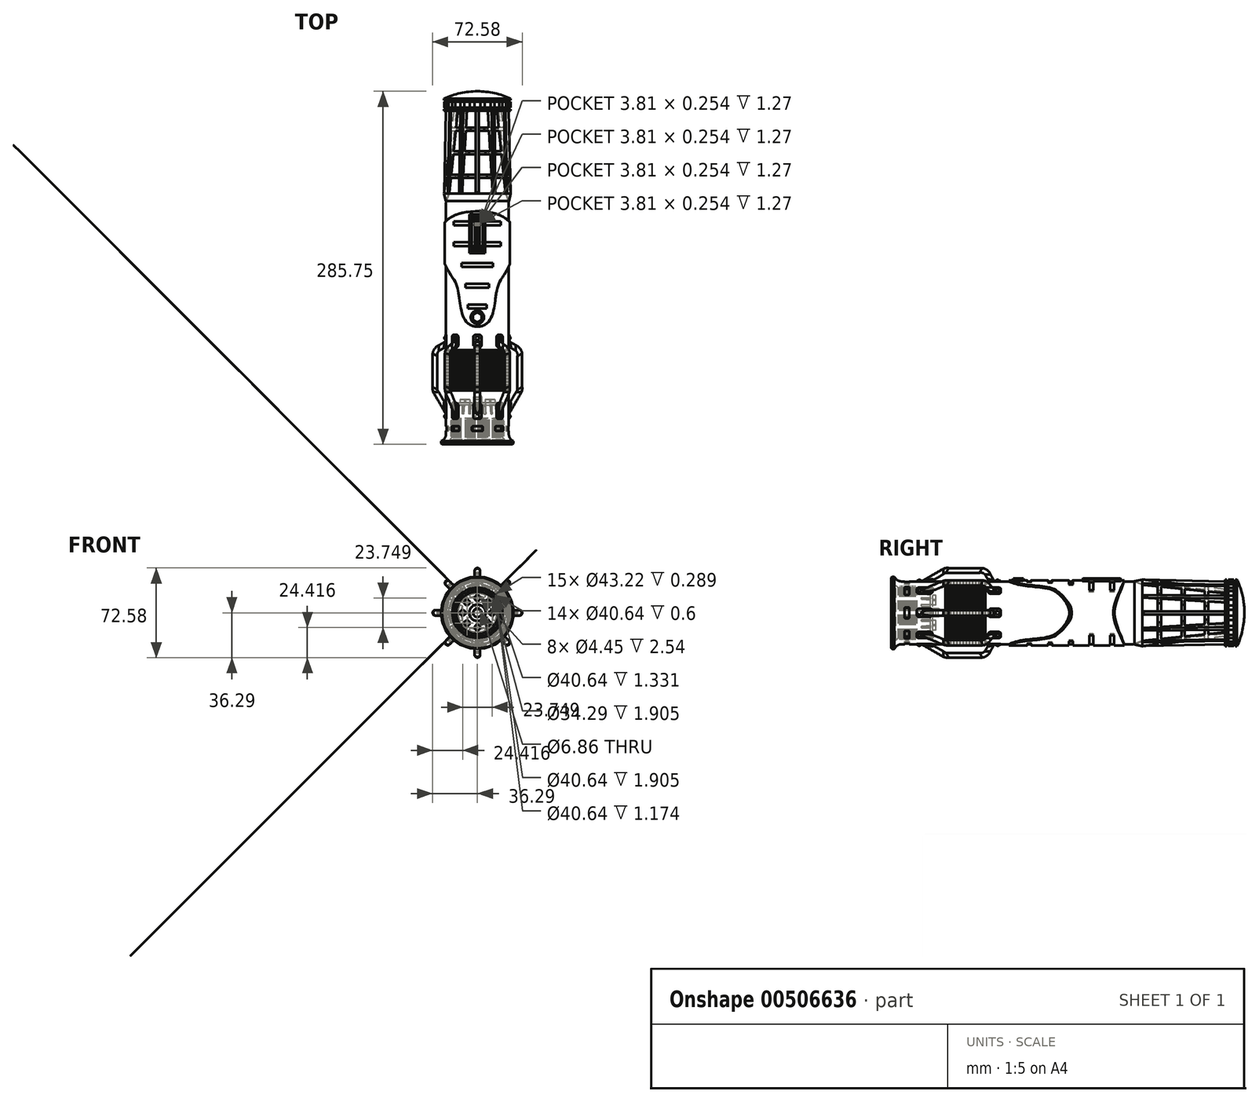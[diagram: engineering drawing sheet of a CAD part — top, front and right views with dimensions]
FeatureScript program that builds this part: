
annotation { "Feature Type Name" : "Feature", "Feature Type Description" : "" }
export const myFeature = defineFeature(function(context is Context, id is Id, definition is map)
    precondition{}
    {
        {
            var Q0;
            Q0=qCreatedBy(makeId("Right.planeOp"),FACE);
            var sketch = newSketch(context, id + "F0", { "sketchPlane" : qUnion([Q0])});
            skLineSegment(sketch, "E0", {"start": v(44.04, 0) * mm, "end": v(254, 0) * mm});
            skLineSegment(sketch, "E1", {"start": v(270.13, 19.05) * mm, "end": v(256.42, 20.68) * mm});
            skLineSegment(sketch, "E2", {"start": v(203, 27.02) * mm, "end": v(196.97, 25.65) * mm});
            skLineSegment(sketch, "E3", {"start": v(195.42, 25.4) * mm, "end": v(76.16, 25.4) * mm});
            skLineSegment(sketch, "E4", {"start": v(0, 25.4) * mm, "end": v(0, 20.32) * mm});
            skLineSegment(sketch, "E5", {"start": v(254, 0) * mm, "end": v(285.75, 0) * mm});
            skPoint(sketch, "E6.visualSharp", {"position": v(270.13, 19.05) * mm});
            skLineSegment(sketch, "E7", {"start": v(0, 25.4) * mm, "end": v(0, 29.21) * mm});
            skLineSegment(sketch, "E8", {"start": v(0, 29.21) * mm, "end": v(2.54, 29.21) * mm});
            skLineSegment(sketch, "E9", {"start": v(2.54, 29.21) * mm, "end": v(4.74, 25.4) * mm});
            skLineSegment(sketch, "E10", {"start": v(31.75, 3.43) * mm, "end": v(31.75, 6.6) * mm});
            skLineSegment(sketch, "E11", {"start": v(20.95, 20.32) * mm, "end": v(19.62, 20.32) * mm});
            skLineSegment(sketch, "E12", {"start": v(1.9, 20.32) * mm, "end": v(3.8, 22.23) * mm});
            skLineSegment(sketch, "E13", {"start": v(3.81, 22.23) * mm, "end": v(5.72, 20.32) * mm});
            skLineSegment(sketch, "E14", {"start": v(6.89, 20.32) * mm, "end": v(6.89, 21.61) * mm});
            skLineSegment(sketch, "E15", {"start": v(6.89, 21.61) * mm, "end": v(7.18, 21.61) * mm});
            skLineSegment(sketch, "E16", {"start": v(7.18, 21.61) * mm, "end": v(7.18, 20.32) * mm});
            skLineSegment(sketch, "E17.1.0.0", {"start": v(7.78, 20.32) * mm, "end": v(7.78, 21.61) * mm});
            skLineSegment(sketch, "E17.1.0.1", {"start": v(7.78, 21.61) * mm, "end": v(8.07, 21.61) * mm});
            skLineSegment(sketch, "E17.1.0.2", {"start": v(8.07, 21.61) * mm, "end": v(8.07, 20.32) * mm});
            skLineSegment(sketch, "E17.2.0.0", {"start": v(8.67, 20.32) * mm, "end": v(8.67, 21.61) * mm});
            skLineSegment(sketch, "E17.2.0.1", {"start": v(8.67, 21.61) * mm, "end": v(8.96, 21.61) * mm});
            skLineSegment(sketch, "E17.2.0.2", {"start": v(8.96, 21.61) * mm, "end": v(8.96, 20.32) * mm});
            skLineSegment(sketch, "E17.3.0.0", {"start": v(9.56, 20.32) * mm, "end": v(9.56, 21.61) * mm});
            skLineSegment(sketch, "E17.3.0.1", {"start": v(9.56, 21.61) * mm, "end": v(9.85, 21.61) * mm});
            skLineSegment(sketch, "E17.3.0.2", {"start": v(9.85, 21.61) * mm, "end": v(9.85, 20.32) * mm});
            skLineSegment(sketch, "E17.4.0.0", {"start": v(10.45, 20.32) * mm, "end": v(10.45, 21.61) * mm});
            skLineSegment(sketch, "E17.4.0.1", {"start": v(10.45, 21.61) * mm, "end": v(10.73, 21.61) * mm});
            skLineSegment(sketch, "E17.4.0.2", {"start": v(10.73, 21.61) * mm, "end": v(10.73, 20.32) * mm});
            skLineSegment(sketch, "E17.5.0.0", {"start": v(11.33, 20.32) * mm, "end": v(11.33, 21.61) * mm});
            skLineSegment(sketch, "E17.5.0.1", {"start": v(11.33, 21.61) * mm, "end": v(11.62, 21.61) * mm});
            skLineSegment(sketch, "E17.5.0.2", {"start": v(11.62, 21.61) * mm, "end": v(11.62, 20.32) * mm});
            skLineSegment(sketch, "E17.6.0.0", {"start": v(12.22, 20.32) * mm, "end": v(12.22, 21.61) * mm});
            skLineSegment(sketch, "E17.6.0.1", {"start": v(12.22, 21.61) * mm, "end": v(12.51, 21.61) * mm});
            skLineSegment(sketch, "E17.6.0.2", {"start": v(12.51, 21.61) * mm, "end": v(12.51, 20.32) * mm});
            skLineSegment(sketch, "E17.7.0.0", {"start": v(13.11, 20.32) * mm, "end": v(13.11, 21.61) * mm});
            skLineSegment(sketch, "E17.7.0.1", {"start": v(13.11, 21.61) * mm, "end": v(13.4, 21.61) * mm});
            skLineSegment(sketch, "E17.7.0.2", {"start": v(13.4, 21.61) * mm, "end": v(13.4, 20.32) * mm});
            skLineSegment(sketch, "E17.8.0.0", {"start": v(14, 20.32) * mm, "end": v(14, 21.61) * mm});
            skLineSegment(sketch, "E17.8.0.1", {"start": v(14, 21.61) * mm, "end": v(14.3, 21.61) * mm});
            skLineSegment(sketch, "E17.8.0.2", {"start": v(14.3, 21.61) * mm, "end": v(14.3, 20.32) * mm});
            skLineSegment(sketch, "E17.9.0.0", {"start": v(14.9, 20.32) * mm, "end": v(14.9, 21.61) * mm});
            skLineSegment(sketch, "E17.9.0.1", {"start": v(14.9, 21.61) * mm, "end": v(15.18, 21.61) * mm});
            skLineSegment(sketch, "E17.9.0.2", {"start": v(15.18, 21.61) * mm, "end": v(15.18, 20.32) * mm});
            skLineSegment(sketch, "E17.10.0.0", {"start": v(15.78, 20.32) * mm, "end": v(15.78, 21.61) * mm});
            skLineSegment(sketch, "E17.10.0.1", {"start": v(15.78, 21.61) * mm, "end": v(16.07, 21.61) * mm});
            skLineSegment(sketch, "E17.10.0.2", {"start": v(16.07, 21.61) * mm, "end": v(16.07, 20.32) * mm});
            skLineSegment(sketch, "E17.11.0.0", {"start": v(16.67, 20.32) * mm, "end": v(16.67, 21.61) * mm});
            skLineSegment(sketch, "E17.11.0.1", {"start": v(16.67, 21.61) * mm, "end": v(16.96, 21.61) * mm});
            skLineSegment(sketch, "E17.11.0.2", {"start": v(16.96, 21.61) * mm, "end": v(16.96, 20.32) * mm});
            skLineSegment(sketch, "E17.12.0.0", {"start": v(17.56, 20.32) * mm, "end": v(17.56, 21.61) * mm});
            skLineSegment(sketch, "E17.12.0.1", {"start": v(17.56, 21.61) * mm, "end": v(17.85, 21.61) * mm});
            skLineSegment(sketch, "E17.12.0.2", {"start": v(17.85, 21.61) * mm, "end": v(17.85, 20.32) * mm});
            skLineSegment(sketch, "E17.13.0.0", {"start": v(18.45, 20.32) * mm, "end": v(18.45, 21.61) * mm});
            skLineSegment(sketch, "E17.13.0.1", {"start": v(18.45, 21.61) * mm, "end": v(18.74, 21.61) * mm});
            skLineSegment(sketch, "E17.13.0.2", {"start": v(18.74, 21.61) * mm, "end": v(18.74, 20.32) * mm});
            skLineSegment(sketch, "E17.14.0.0", {"start": v(19.34, 20.32) * mm, "end": v(19.34, 21.61) * mm});
            skLineSegment(sketch, "E17.14.0.1", {"start": v(19.34, 21.61) * mm, "end": v(19.62, 21.61) * mm});
            skLineSegment(sketch, "E17.14.0.2", {"start": v(19.62, 21.61) * mm, "end": v(19.62, 20.32) * mm});
            skLineSegment(sketch, "E17.direction1", {"start": v(7.18, 20.32) * mm, "end": v(7.78, 20.32) * mm, "construction": true});
            skLineSegment(sketch, "E18", {"start": v(31.75, 3.43) * mm, "end": v(38.1, 3.43) * mm});
            skLineSegment(sketch, "E19", {"start": v(38.1, 3.43) * mm, "end": v(44.04, 0) * mm});
            skLineSegment(sketch, "E20.bottom", {"start": v(31.75, 17.15) * mm, "end": v(33.65, 17.15) * mm});
            skLineSegment(sketch, "E20.top", {"start": v(31.75, 6.6) * mm, "end": v(33.65, 6.6) * mm});
            skLineSegment(sketch, "E20.right", {"start": v(33.65, 17.15) * mm, "end": v(33.65, 6.6) * mm});
            skLineSegment(sketch, "E21", {"start": v(31.75, 18.42) * mm, "end": v(20.95, 20.32) * mm});
            skPoint(sketch, "E22.orphan", {"position": v(31.75, 20.32) * mm});
            skLineSegment(sketch, "E23.trimOffspring", {"start": v(31.75, 17.15) * mm, "end": v(31.75, 18.42) * mm});
            skLineSegment(sketch, "E24.trimOffspring", {"start": v(6.89, 20.32) * mm, "end": v(5.71, 20.32) * mm});
            skLineSegment(sketch, "E25.trimOffspring", {"start": v(7.78, 20.32) * mm, "end": v(7.18, 20.32) * mm});
            skLineSegment(sketch, "E26.trimOffspring", {"start": v(8.67, 20.32) * mm, "end": v(8.07, 20.32) * mm});
            skLineSegment(sketch, "E27.trimOffspring", {"start": v(9.56, 20.32) * mm, "end": v(8.96, 20.32) * mm});
            skLineSegment(sketch, "E28.trimOffspring", {"start": v(10.45, 20.32) * mm, "end": v(9.85, 20.32) * mm});
            skLineSegment(sketch, "E29.trimOffspring", {"start": v(11.33, 20.32) * mm, "end": v(10.73, 20.32) * mm});
            skLineSegment(sketch, "E30.trimOffspring", {"start": v(12.22, 20.32) * mm, "end": v(11.62, 20.32) * mm});
            skLineSegment(sketch, "E31.trimOffspring", {"start": v(13.11, 20.32) * mm, "end": v(12.51, 20.32) * mm});
            skLineSegment(sketch, "E32.trimOffspring", {"start": v(14, 20.32) * mm, "end": v(13.4, 20.32) * mm});
            skLineSegment(sketch, "E33.trimOffspring", {"start": v(14.9, 20.32) * mm, "end": v(14.3, 20.32) * mm});
            skLineSegment(sketch, "E34.trimOffspring", {"start": v(15.78, 20.32) * mm, "end": v(15.18, 20.32) * mm});
            skLineSegment(sketch, "E35.trimOffspring", {"start": v(16.67, 20.32) * mm, "end": v(16.07, 20.32) * mm});
            skLineSegment(sketch, "E36.trimOffspring", {"start": v(17.56, 20.32) * mm, "end": v(16.96, 20.32) * mm});
            skLineSegment(sketch, "E37.trimOffspring", {"start": v(18.45, 20.32) * mm, "end": v(17.85, 20.32) * mm});
            skLineSegment(sketch, "E38.trimOffspring", {"start": v(19.34, 20.32) * mm, "end": v(18.74, 20.32) * mm});
            skLineSegment(sketch, "E39.trimOffspring", {"start": v(1.9, 20.32) * mm, "end": v(0, 20.32) * mm});
            skPoint(sketch, "E40.orphan", {"position": v(0, 0) * mm});
            skLineSegment(sketch, "E41.top", {"start": v(44.04, 26.04) * mm, "end": v(45.3, 26.04) * mm});
            skLineSegment(sketch, "E42", {"start": v(44.04, 26.04) * mm, "end": v(43.67, 25.4) * mm});
            skLineSegment(sketch, "E43", {"start": v(75.79, 26.04) * mm, "end": v(76.16, 25.4) * mm});
            skLineSegment(sketch, "E44", {"start": v(45.3, 26.03) * mm, "end": v(45.3, 26.1) * mm});
            skLineSegment(sketch, "E45", {"start": v(45.82, 26.1) * mm, "end": v(45.82, 26.03) * mm});
            skArc(sketch, "E46", {"start": v(45.82, 26.1) * mm, "mid": v(45.56, 26.35) * mm, "end": v(45.3, 26.1) * mm});
            skLineSegment(sketch, "E47.1.0.0", {"start": v(47.85, 26.04) * mm, "end": v(47.85, 26.1) * mm});
            skArc(sketch, "E47.1.0.1", {"start": v(48.36, 26.1) * mm, "mid": v(48.1, 26.35) * mm, "end": v(47.85, 26.1) * mm});
            skLineSegment(sketch, "E47.1.0.2", {"start": v(48.36, 26.1) * mm, "end": v(48.36, 26.04) * mm});
            skLineSegment(sketch, "E47.2.0.0", {"start": v(50.39, 26.04) * mm, "end": v(50.39, 26.1) * mm});
            skArc(sketch, "E47.2.0.1", {"start": v(50.9, 26.1) * mm, "mid": v(50.64, 26.35) * mm, "end": v(50.39, 26.1) * mm});
            skLineSegment(sketch, "E47.2.0.2", {"start": v(50.9, 26.1) * mm, "end": v(50.9, 26.04) * mm});
            skLineSegment(sketch, "E47.3.0.0", {"start": v(52.93, 26.04) * mm, "end": v(52.93, 26.1) * mm});
            skArc(sketch, "E47.3.0.1", {"start": v(53.44, 26.1) * mm, "mid": v(53.18, 26.35) * mm, "end": v(52.93, 26.1) * mm});
            skLineSegment(sketch, "E47.3.0.2", {"start": v(53.44, 26.1) * mm, "end": v(53.44, 26.04) * mm});
            skLineSegment(sketch, "E47.4.0.0", {"start": v(55.47, 26.04) * mm, "end": v(55.47, 26.1) * mm});
            skArc(sketch, "E47.4.0.1", {"start": v(55.98, 26.1) * mm, "mid": v(55.72, 26.35) * mm, "end": v(55.47, 26.1) * mm});
            skLineSegment(sketch, "E47.4.0.2", {"start": v(55.98, 26.1) * mm, "end": v(55.98, 26.04) * mm});
            skLineSegment(sketch, "E47.5.0.0", {"start": v(58, 26.04) * mm, "end": v(58, 26.1) * mm});
            skArc(sketch, "E47.5.0.1", {"start": v(58.52, 26.1) * mm, "mid": v(58.26, 26.35) * mm, "end": v(58, 26.1) * mm});
            skLineSegment(sketch, "E47.5.0.2", {"start": v(58.52, 26.1) * mm, "end": v(58.52, 26.04) * mm});
            skLineSegment(sketch, "E47.6.0.0", {"start": v(60.55, 26.04) * mm, "end": v(60.55, 26.1) * mm});
            skArc(sketch, "E47.6.0.1", {"start": v(61.06, 26.1) * mm, "mid": v(60.8, 26.35) * mm, "end": v(60.55, 26.1) * mm});
            skLineSegment(sketch, "E47.6.0.2", {"start": v(61.06, 26.1) * mm, "end": v(61.06, 26.04) * mm});
            skLineSegment(sketch, "E47.7.0.0", {"start": v(63.09, 26.04) * mm, "end": v(63.09, 26.1) * mm});
            skArc(sketch, "E47.7.0.1", {"start": v(63.6, 26.1) * mm, "mid": v(63.34, 26.35) * mm, "end": v(63.09, 26.1) * mm});
            skLineSegment(sketch, "E47.7.0.2", {"start": v(63.6, 26.1) * mm, "end": v(63.6, 26.04) * mm});
            skLineSegment(sketch, "E47.8.0.0", {"start": v(65.63, 26.04) * mm, "end": v(65.63, 26.1) * mm});
            skArc(sketch, "E47.8.0.1", {"start": v(66.14, 26.1) * mm, "mid": v(65.88, 26.35) * mm, "end": v(65.63, 26.1) * mm});
            skLineSegment(sketch, "E47.8.0.2", {"start": v(66.14, 26.1) * mm, "end": v(66.14, 26.04) * mm});
            skLineSegment(sketch, "E47.9.0.0", {"start": v(68.17, 26.04) * mm, "end": v(68.17, 26.1) * mm});
            skArc(sketch, "E47.9.0.1", {"start": v(68.68, 26.1) * mm, "mid": v(68.42, 26.35) * mm, "end": v(68.17, 26.1) * mm});
            skLineSegment(sketch, "E47.9.0.2", {"start": v(68.68, 26.1) * mm, "end": v(68.68, 26.04) * mm});
            skLineSegment(sketch, "E47.10.0.0", {"start": v(70.7, 26.04) * mm, "end": v(70.7, 26.1) * mm});
            skArc(sketch, "E47.10.0.1", {"start": v(71.22, 26.1) * mm, "mid": v(70.96, 26.35) * mm, "end": v(70.7, 26.1) * mm});
            skLineSegment(sketch, "E47.10.0.2", {"start": v(71.22, 26.1) * mm, "end": v(71.22, 26.04) * mm});
            skLineSegment(sketch, "E47.11.0.0", {"start": v(73.25, 26.04) * mm, "end": v(73.25, 26.1) * mm});
            skArc(sketch, "E47.11.0.1", {"start": v(73.76, 26.1) * mm, "mid": v(73.5, 26.35) * mm, "end": v(73.25, 26.1) * mm});
            skLineSegment(sketch, "E47.11.0.2", {"start": v(73.76, 26.1) * mm, "end": v(73.76, 26.03) * mm});
            skLineSegment(sketch, "E47.direction1", {"start": v(45.3, 26.04) * mm, "end": v(47.85, 26.04) * mm, "construction": true});
            skLineSegment(sketch, "E48.trimOffspring", {"start": v(45.82, 26.04) * mm, "end": v(47.85, 26.04) * mm});
            skLineSegment(sketch, "E49.trimOffspring", {"start": v(48.36, 26.04) * mm, "end": v(50.39, 26.04) * mm});
            skLineSegment(sketch, "E50.trimOffspring", {"start": v(50.9, 26.04) * mm, "end": v(52.93, 26.04) * mm});
            skLineSegment(sketch, "E51.trimOffspring", {"start": v(53.44, 26.04) * mm, "end": v(55.47, 26.04) * mm});
            skLineSegment(sketch, "E52.trimOffspring", {"start": v(55.98, 26.04) * mm, "end": v(58, 26.04) * mm});
            skLineSegment(sketch, "E53.trimOffspring", {"start": v(58.52, 26.04) * mm, "end": v(60.55, 26.04) * mm});
            skLineSegment(sketch, "E54.trimOffspring", {"start": v(61.06, 26.04) * mm, "end": v(63.09, 26.04) * mm});
            skLineSegment(sketch, "E55.trimOffspring", {"start": v(63.6, 26.04) * mm, "end": v(65.63, 26.04) * mm});
            skLineSegment(sketch, "E56.trimOffspring", {"start": v(66.14, 26.04) * mm, "end": v(68.17, 26.04) * mm});
            skLineSegment(sketch, "E57.trimOffspring", {"start": v(68.68, 26.04) * mm, "end": v(70.7, 26.04) * mm});
            skLineSegment(sketch, "E58.trimOffspring", {"start": v(71.22, 26.04) * mm, "end": v(73.25, 26.04) * mm});
            skLineSegment(sketch, "E59.trimOffspring", {"start": v(73.76, 26.04) * mm, "end": v(75.79, 26.04) * mm});
            skLineSegment(sketch, "E60.trimOffspring", {"start": v(43.67, 25.4) * mm, "end": v(4.74, 25.4) * mm});
            skPoint(sketch, "E41.left.start.orphan", {"position": v(44.04, 25.4) * mm});
            skLineSegment(sketch, "E61", {"start": v(196.3, 25.25) * mm, "end": v(203.03, 22.8) * mm});
            skLineSegment(sketch, "E62", {"start": v(203.03, 22.8) * mm, "end": v(203.03, 23.2) * mm});
            skLineSegment(sketch, "E63", {"start": v(203.03, 23.2) * mm, "end": v(196.96, 25.4) * mm});
            skPoint(sketch, "E64.visualSharp", {"position": v(195.87, 25.4) * mm});
            skArc(sketch, "E64.filletArc", {"start": v(196.3, 25.25) * mm, "mid": v(195.86, 25.36) * mm, "end": v(195.42, 25.4) * mm});
            skPoint(sketch, "E65.visualSharp", {"position": v(196.55, 25.56) * mm});
            skArc(sketch, "E65.filletArc", {"start": v(196.97, 25.65) * mm, "mid": v(196.88, 25.54) * mm, "end": v(196.96, 25.4) * mm});
            skArc(sketch, "E66", {"start": v(285.75, 0) * mm, "mid": v(284.22, 13.84) * mm, "end": v(279.71, 27.02) * mm});
            skLineSegment(sketch, "E67", {"start": v(270.13, 19.05) * mm, "end": v(270.13, 27.02) * mm});
            skLineSegment(sketch, "E68", {"start": v(270.13, 27.02) * mm, "end": v(271.4, 27.02) * mm});
            skLineSegment(sketch, "E69", {"start": v(271.4, 27.02) * mm, "end": v(271.4, 24.86) * mm});
            skLineSegment(sketch, "E70", {"start": v(271.4, 24.86) * mm, "end": v(272.67, 24.86) * mm});
            skLineSegment(sketch, "E71", {"start": v(272.67, 24.86) * mm, "end": v(272.67, 27.02) * mm});
            skLineSegment(sketch, "E72", {"start": v(272.67, 27.02) * mm, "end": v(277.17, 27.02) * mm});
            skLineSegment(sketch, "E73", {"start": v(277.17, 27.02) * mm, "end": v(277.17, 24.86) * mm});
            skLineSegment(sketch, "E74", {"start": v(277.17, 24.86) * mm, "end": v(278.44, 24.86) * mm});
            skLineSegment(sketch, "E75", {"start": v(278.44, 24.86) * mm, "end": v(278.44, 27.02) * mm});
            skLineSegment(sketch, "E76.trimOffspring", {"start": v(278.44, 27.02) * mm, "end": v(279.71, 27.02) * mm});
            skLineSegment(sketch, "E77.top", {"start": v(215.7, 17.9) * mm, "end": v(218.32, 17.9) * mm});
            skLineSegment(sketch, "E77.left", {"start": v(215.7, 25.51) * mm, "end": v(215.7, 17.9) * mm});
            skLineSegment(sketch, "E77.right", {"start": v(218.32, 25.2) * mm, "end": v(218.32, 17.9) * mm});
            skLineSegment(sketch, "E78.1.0.0", {"start": v(234.75, 23.25) * mm, "end": v(234.75, 15.63) * mm});
            skLineSegment(sketch, "E78.1.0.1", {"start": v(237.37, 22.94) * mm, "end": v(237.37, 15.63) * mm});
            skLineSegment(sketch, "E78.1.0.2", {"start": v(234.75, 15.63) * mm, "end": v(237.37, 15.63) * mm});
            skLineSegment(sketch, "E78.2.0.0", {"start": v(253.8, 20.99) * mm, "end": v(253.8, 13.37) * mm});
            skLineSegment(sketch, "E78.2.0.1", {"start": v(256.42, 20.68) * mm, "end": v(256.42, 13.37) * mm});
            skLineSegment(sketch, "E78.2.0.2", {"start": v(253.8, 13.37) * mm, "end": v(256.42, 13.37) * mm});
            skLineSegment(sketch, "E79.trimOffspring", {"start": v(215.7, 25.51) * mm, "end": v(203, 27.02) * mm});
            skPoint(sketch, "E80.orphan", {"position": v(218.32, 26.14) * mm});
            skPoint(sketch, "E81.orphan", {"position": v(215.7, 29.67) * mm});
            skPoint(sketch, "E82.orphan", {"position": v(234.75, 29.67) * mm});
            skPoint(sketch, "E83.orphan", {"position": v(237.37, 24.63) * mm});
            skLineSegment(sketch, "E84.trimOffspring", {"start": v(234.75, 23.25) * mm, "end": v(218.32, 25.2) * mm});
            skPoint(sketch, "E85.orphan", {"position": v(253.8, 28.16) * mm});
            skLineSegment(sketch, "E86.trimOffspring", {"start": v(253.8, 20.99) * mm, "end": v(237.37, 22.94) * mm});
            skPoint(sketch, "E87.orphan", {"position": v(256.42, 22.37) * mm});
            skSolve(sketch);
        }
        {
            var Q0;
            Q0=qSketchRegion(id+"F0",true);
            var Q1;
            Q1=sQuery(id+"F0.wireOp",EDGE,"E0");
            revolve(context, id + "F1", {"entities" : qUnion([Q0]), "axis" : qUnion([Q1]), "revolveType" : RevolveType.FULL});
        }
        {
            var Q0;
            Q0=qCreatedBy(makeId("Top.planeOp"),FACE);
            var sketch = newSketch(context, id + "F2", { "sketchPlane" : qUnion([Q0])});
            skFitSpline(sketch, "E88", {"points": [v(0, 95.25) * mm, v(18.97, 133.22) * mm], "startDerivative": vector(53.75, 1.68) * mm, "endDerivative": vector(22.66, 34.25) * mm});
            skFitSpline(sketch, "E89", {"points": [v(18.97, 133.22) * mm, v(0, 188.6) * mm], "startDerivative": vector(48.26, 68.65) * mm, "endDerivative": vector(-122.9, 0.45) * mm});
            skLineSegment(sketch, "E90.bottom", {"start": v(0, 180.34) * mm, "end": v(19.05, 180.34) * mm});
            skLineSegment(sketch, "E90.top", {"start": v(0, 177.16) * mm, "end": v(19.05, 177.16) * mm});
            skLineSegment(sketch, "E90.right", {"start": v(19.05, 180.34) * mm, "end": v(19.05, 177.16) * mm});
            skLineSegment(sketch, "E91.bottom", {"start": v(0, 163.58) * mm, "end": v(19.05, 163.58) * mm});
            skLineSegment(sketch, "E91.top", {"start": v(0, 160.4) * mm, "end": v(19.05, 160.4) * mm});
            skLineSegment(sketch, "E91.right", {"start": v(19.05, 163.58) * mm, "end": v(19.05, 160.4) * mm});
            skLineSegment(sketch, "E92.bottom", {"start": v(0, 146.81) * mm, "end": v(12.7, 146.81) * mm});
            skLineSegment(sketch, "E92.top", {"start": v(0, 143.64) * mm, "end": v(12.7, 143.64) * mm});
            skLineSegment(sketch, "E92.right", {"start": v(12.7, 146.81) * mm, "end": v(12.7, 143.64) * mm});
            skLineSegment(sketch, "E93.bottom", {"start": v(0, 130.05) * mm, "end": v(9.53, 130.05) * mm});
            skLineSegment(sketch, "E93.top", {"start": v(0, 126.87) * mm, "end": v(9.53, 126.87) * mm});
            skLineSegment(sketch, "E93.right", {"start": v(9.53, 130.05) * mm, "end": v(9.53, 126.87) * mm});
            skLineSegment(sketch, "E94.bottom", {"start": v(0, 113.28) * mm, "end": v(7.62, 113.28) * mm});
            skLineSegment(sketch, "E94.top", {"start": v(0, 110.1) * mm, "end": v(7.62, 110.1) * mm});
            skLineSegment(sketch, "E94.right", {"start": v(7.62, 113.28) * mm, "end": v(7.62, 110.1) * mm});
            skPoint(sketch, "E95.orphan", {"position": v(9.53, 110.1) * mm});
            skFitSpline(sketch, "E96.MirrorCS", {"points": [v(-18.97, 133.22) * mm, v(0, 188.6) * mm], "startDerivative": vector(-48.26, 68.65) * mm, "endDerivative": vector(122.9, 0.45) * mm});
            skFitSpline(sketch, "E97.MirrorCS", {"points": [v(0, 95.25) * mm, v(-18.97, 133.22) * mm], "startDerivative": vector(-53.75, 1.68) * mm, "endDerivative": vector(-22.66, 34.25) * mm});
            skLineSegment(sketch, "E98.MirrorCS", {"start": v(0, 110.1) * mm, "end": v(-7.62, 110.1) * mm});
            skLineSegment(sketch, "E99.MirrorCS", {"start": v(-7.62, 113.28) * mm, "end": v(-7.62, 110.1) * mm});
            skLineSegment(sketch, "E100.MirrorCS", {"start": v(0, 113.28) * mm, "end": v(-7.62, 113.28) * mm});
            skLineSegment(sketch, "E101.MirrorCS", {"start": v(0, 126.87) * mm, "end": v(-9.53, 126.87) * mm});
            skLineSegment(sketch, "E102.MirrorCS", {"start": v(-9.53, 130.05) * mm, "end": v(-9.53, 126.87) * mm});
            skLineSegment(sketch, "E103.MirrorCS", {"start": v(0, 130.05) * mm, "end": v(-9.53, 130.05) * mm});
            skLineSegment(sketch, "E104.MirrorCS", {"start": v(0, 143.64) * mm, "end": v(-12.7, 143.64) * mm});
            skLineSegment(sketch, "E105.MirrorCS", {"start": v(-12.7, 146.81) * mm, "end": v(-12.7, 143.64) * mm});
            skLineSegment(sketch, "E106.MirrorCS", {"start": v(0, 146.81) * mm, "end": v(-12.7, 146.81) * mm});
            skLineSegment(sketch, "E107.MirrorCS", {"start": v(0, 160.4) * mm, "end": v(-19.05, 160.4) * mm});
            skLineSegment(sketch, "E108.MirrorCS", {"start": v(-19.05, 163.58) * mm, "end": v(-19.05, 160.4) * mm});
            skLineSegment(sketch, "E109.MirrorCS", {"start": v(0, 163.58) * mm, "end": v(-19.05, 163.58) * mm});
            skLineSegment(sketch, "E110.MirrorCS", {"start": v(0, 177.16) * mm, "end": v(-19.05, 177.16) * mm});
            skLineSegment(sketch, "E111.MirrorCS", {"start": v(-19.05, 180.34) * mm, "end": v(-19.05, 177.16) * mm});
            skLineSegment(sketch, "E112.MirrorCS", {"start": v(0, 180.34) * mm, "end": v(-19.05, 180.34) * mm});
            skSolve(sketch);
        }
        {
            var Q0;
            Q0=qSketchRegion(id+"F2",true);
            extrude(context, id + "F3", {"entities" : qUnion([Q0]), "operationType" : NewBodyOperationType.ADD, "depth" : 30.48 * mm, "hasSecondDirection" : true, "secondDirectionOppositeDirection" : true, "secondDirectionDepth" : 30.48 * mm});
        }
        {
            var Q0;
            Q0=qCreatedBy(makeId("Front.planeOp"),FACE);
            cPlane(context, id + "F4", {"entities" : qUnion([Q0]), "cplaneType" : CPlaneType.OFFSET, "offset" : 91.44 * mm, "oppositeDirection" : true, "width" : 152.4 * mm, "height" : 152.4 * mm});
        }
        {
            var Q0;
            Q0=qCreatedBy(id+"F4.planeOp",FACE);
            var sketch = newSketch(context, id + "F5", { "sketchPlane" : qUnion([Q0])});
            skCircle(sketch, "E113", {"center": v(0, 0) * mm, "radius": 26.35 * mm});
            skCircle(sketch, "E114", {"center": v(0, 0) * mm, "radius": 49.48 * mm});
            skSolve(sketch);
        }
        {
            var Q0;
            Q0=qSketchRegion(id+"F5",true);
            extrude(context, id + "F6", {"entities" : qUnion([Q0]), "operationType" : NewBodyOperationType.REMOVE, "oppositeDirection" : true, "depth" : 99.06 * mm});
        }
        {
            var Q0;
            Q0=qCreatedBy(makeId("Right.planeOp"),FACE);
            var sketch = newSketch(context, id + "F7", { "sketchPlane" : qUnion([Q0])});
            skLineSegment(sketch, "E115", {"start": v(23.88, 22.86) * mm, "end": v(42.2, 33.44) * mm});
            skLineSegment(sketch, "E116", {"start": v(45.37, 34.3) * mm, "end": v(72.49, 34.3) * mm});
            skLineSegment(sketch, "E117", {"start": v(77.99, 31.11) * mm, "end": v(82.75, 22.86) * mm});
            skPoint(sketch, "E118.visualSharp", {"position": v(76.16, 34.3) * mm});
            skArc(sketch, "E118.filletArc", {"start": v(77.99, 31.12) * mm, "mid": v(75.66, 33.44) * mm, "end": v(72.49, 34.3) * mm});
            skPoint(sketch, "E119.visualSharp", {"position": v(43.67, 34.3) * mm});
            skArc(sketch, "E119.filletArc", {"start": v(45.37, 34.3) * mm, "mid": v(43.73, 34.07) * mm, "end": v(42.2, 33.44) * mm});
            skSolve(sketch);
        }
        {
            var Q0;
            Q0=qCreatedBy(makeId("Top.planeOp"),FACE);
            cPlane(context, id + "F8", {"entities" : qUnion([Q0]), "cplaneType" : CPlaneType.OFFSET, "offset" : 22.86 * mm, "width" : 152.4 * mm, "height" : 152.4 * mm});
        }
        {
            var Q0;
            Q0=qCreatedBy(id+"F8.planeOp",FACE);
            var sketch = newSketch(context, id + "F9", { "sketchPlane" : qUnion([Q0])});
            skCircle(sketch, "E120", {"center": v(0, 82.75) * mm, "radius": 2.22 * mm});
            skSolve(sketch);
        }
        {
            var Q0;
            Q0=qSketchRegion(id+"F9",true);
            var Q1;
            Q1=qConstructionFilter(qBodyType(qCreatedBy(id+"F7",EDGE),BodyType.WIRE),ConstructionObject.NO);
            sweep(context, id + "F10", {"profiles" : qUnion([Q0]), "path" : qUnion([Q1])});
        }
        {
            var Q0;
            Q0=qCreatedBy(makeId("Right.planeOp"),FACE);
            var sketch = newSketch(context, id + "F11", { "sketchPlane" : qUnion([Q0])});
            skLineSegment(sketch, "E121.bottom", {"start": v(20.62, 24.56) * mm, "end": v(33.32, 24.56) * mm});
            skLineSegment(sketch, "E121.top", {"start": v(20.62, 25.78) * mm, "end": v(33.32, 25.78) * mm});
            skLineSegment(sketch, "E121.left", {"start": v(20.62, 24.56) * mm, "end": v(20.62, 25.78) * mm});
            skLineSegment(sketch, "E121.right", {"start": v(33.32, 24.56) * mm, "end": v(33.32, 25.78) * mm});
            skLineSegment(sketch, "E122.bottom", {"start": v(78.5, 24.26) * mm, "end": v(88.67, 24.26) * mm});
            skLineSegment(sketch, "E122.top", {"start": v(78.5, 25.78) * mm, "end": v(88.67, 25.78) * mm});
            skLineSegment(sketch, "E122.left", {"start": v(78.5, 24.26) * mm, "end": v(78.5, 25.78) * mm});
            skLineSegment(sketch, "E122.right", {"start": v(88.67, 24.26) * mm, "end": v(88.67, 25.78) * mm});
            skLineSegment(sketch, "E123", {"start": v(0, 0) * mm, "end": v(95.37, 0) * mm});
            skSolve(sketch);
        }
        {
            var Q0;
            Q0=qSketchRegion(id+"F11",true);
            var Q1;
            Q1=sQuery(id+"F11.wireOp",EDGE,"E123");
            revolve(context, id + "F12", {"entities" : qUnion([Q0]), "axis" : qUnion([Q1]), "revolveType" : RevolveType.SYMMETRIC, "angle" : 15 * degree});
        }
        {
            var Q0;
            Q0=makeQuery(id+"F12.opRevolve","CAP_EDGE",EDGE,{"disambiguationData":[OSD([sQuery(id+"F11.wireOp",EDGE,"E121.left")])],"isStart":false});
            var Q1;
            Q1=makeQuery(id+"F12.opRevolve","CAP_EDGE",EDGE,{"disambiguationData":[OSD([sQuery(id+"F11.wireOp",EDGE,"E121.right")])],"isStart":false});
            var Q2;
            Q2=makeQuery(id+"F12.opRevolve","CAP_EDGE",EDGE,{"disambiguationData":[OSD([sQuery(id+"F11.wireOp",EDGE,"E121.left")])],"isStart":true});
            var Q3;
            Q3=makeQuery(id+"F12.opRevolve","CAP_EDGE",EDGE,{"disambiguationData":[OSD([sQuery(id+"F11.wireOp",EDGE,"E121.right")])],"isStart":true});
            var Q4;
            Q4=makeQuery(id+"F12.opRevolve","CAP_EDGE",EDGE,{"disambiguationData":[OSD([sQuery(id+"F11.wireOp",EDGE,"E122.left")])],"isStart":false});
            var Q5;
            Q5=makeQuery(id+"F12.opRevolve","CAP_EDGE",EDGE,{"disambiguationData":[OSD([sQuery(id+"F11.wireOp",EDGE,"E122.left")])],"isStart":true});
            var Q6;
            Q6=makeQuery(id+"F12.opRevolve","CAP_EDGE",EDGE,{"disambiguationData":[OSD([sQuery(id+"F11.wireOp",EDGE,"E122.right")])],"isStart":false});
            var Q7;
            Q7=makeQuery(id+"F12.opRevolve","CAP_EDGE",EDGE,{"disambiguationData":[OSD([sQuery(id+"F11.wireOp",EDGE,"E122.right")])],"isStart":true});
            fillet(context, id + "F13", {"entities" : qUnion([Q0, Q1, Q2, Q3, Q4, Q5, Q6, Q7]), "radius" : 1.9 * mm, "tangentPropagation" : true, "allowEdgeOverflow" : false});
        }
        {
            var Q0;
            Q0=qCreatedBy(makeId("Right.planeOp"),FACE);
            var sketch = newSketch(context, id + "F14", { "sketchPlane" : qUnion([Q0])});
            skLineSegment(sketch, "E124", {"start": v(20.62, 25.78) * mm, "end": v(24.8, 25.78) * mm, "construction": true});
            skArc(sketch, "E125", {"start": v(22.71, 26.73) * mm, "mid": v(21, 25.02) * mm, "end": v(22.71, 23.3) * mm});
            skPoint(sketch, "E125.centerSnap0", {"position": v(22.71, 25.78) * mm});
            skLineSegment(sketch, "E126", {"start": v(22.71, 23.3) * mm, "end": v(22.71, 26.73) * mm});
            skSolve(sketch);
        }
        {
            var Q0;
            Q0=qSketchRegion(id+"F14",true);
            var Q1;
            Q1=sQuery(id+"F14.wireOp",EDGE,"E126");
            revolve(context, id + "F15", {"entities" : qUnion([Q0]), "axis" : qUnion([Q1]), "revolveType" : RevolveType.FULL});
        }
        {
            var Q0;
            Q0=qCreatedBy(makeId("Right.planeOp"),FACE);
            var sketch = newSketch(context, id + "F16", { "sketchPlane" : qUnion([Q0])});
            skLineSegment(sketch, "E127", {"start": v(88.67, 25.78) * mm, "end": v(83.46, 25.78) * mm, "construction": true});
            skArc(sketch, "E128", {"start": v(86.07, 26.73) * mm, "mid": v(84.35, 25.02) * mm, "end": v(86.07, 23.3) * mm});
            skPoint(sketch, "E128.centerSnap0", {"position": v(86.07, 25.78) * mm});
            skLineSegment(sketch, "E129", {"start": v(86.07, 26.73) * mm, "end": v(86.07, 23.3) * mm});
            skSolve(sketch);
        }
        {
            var Q0;
            Q0=qSketchRegion(id+"F16",true);
            var Q1;
            Q1=sQuery(id+"F16.wireOp",EDGE,"E129");
            revolve(context, id + "F17", {"entities" : qUnion([Q0]), "axis" : qUnion([Q1]), "revolveType" : RevolveType.FULL});
        }
        {
            var Q0;
            Q0=makeQuery(id+"F10.opSweep","SWEPT_BODY",BODY,{"disambiguationData":[OSD([sQuery(id+"F7.wireOp",EDGE,"E115"),sQuery(id+"F9.wireOp",EDGE,"E120")])]});
            var Q1;
            Q1=makeQuery(id+"F12.opRevolve","SWEPT_BODY",BODY,{"disambiguationData":[OSD([sQuery(id+"F11.wireOp",EDGE,"E121.bottom"),sQuery(id+"F11.wireOp",EDGE,"E121.top"),sQuery(id+"F11.wireOp",EDGE,"E121.left"),sQuery(id+"F11.wireOp",EDGE,"E121.right")])]});
            var Q2;
            Q2=makeQuery(id+"F15.opRevolve","SWEPT_BODY",BODY,{"disambiguationData":[OSD([sQuery(id+"F14.wireOp",EDGE,"E125"),sQuery(id+"F14.wireOp",EDGE,"E126")])]});
            var Q3;
            Q3=makeQuery(id+"F12.opRevolve","SWEPT_BODY",BODY,{"disambiguationData":[OSD([sQuery(id+"F11.wireOp",EDGE,"E122.bottom"),sQuery(id+"F11.wireOp",EDGE,"E122.top"),sQuery(id+"F11.wireOp",EDGE,"E122.left"),sQuery(id+"F11.wireOp",EDGE,"E122.right")])]});
            var Q4;
            Q4=makeQuery(id+"F17.opRevolve","SWEPT_BODY",BODY,{"disambiguationData":[OSD([sQuery(id+"F16.wireOp",EDGE,"E128"),sQuery(id+"F16.wireOp",EDGE,"E129")])]});
            var Q5;
            Q5=makeQuery(id+"F1.opRevolve","SWEPT_EDGE",EDGE,{"disambiguationData":[OSD([sQuery(id+"F0.wireOp",EDGE,"E7"),sQuery(id+"F0.wireOp",EDGE,"E8")])]});
            circularPattern(context, id + "F18", {"operationType" : NewBodyOperationType.ADD, "entities" : qUnion([Q0, Q1, Q2, Q3, Q4]), "axis" : qUnion([Q5]), "angle" : 45 * degree, "instanceCount" : 8});
        }
        {
            var Q0;
            Q0=qCreatedBy(makeId("Right.planeOp"),FACE);
            var sketch = newSketch(context, id + "F19", { "sketchPlane" : qUnion([Q0])});
            skLineSegment(sketch, "E130", {"start": v(203, 26.92) * mm, "end": v(271.4, 25.4) * mm});
            skLineSegment(sketch, "E131", {"start": v(203, 26.92) * mm, "end": v(203, 11.23) * mm});
            skLineSegment(sketch, "E132", {"start": v(203, 11.23) * mm, "end": v(271.4, 11.23) * mm});
            skLineSegment(sketch, "E133", {"start": v(271.4, 11.23) * mm, "end": v(271.4, 25.4) * mm});
            skSolve(sketch);
        }
        {
            var Q0;
            Q0=qSketchRegion(id+"F19",true);
            extrude(context, id + "F20", {"entities" : qUnion([Q0]), "depth" : 1.27 * mm, "hasSecondDirection" : true, "secondDirectionOppositeDirection" : true, "secondDirectionDepth" : 1.27 * mm});
        }
        {
            var Q0;
            Q0=makeQuery(id+"F20.opExtrude","SWEPT_BODY",BODY,{"disambiguationData":[OSD([sQuery(id+"F19.wireOp",EDGE,"E130"),sQuery(id+"F19.wireOp",EDGE,"E131"),sQuery(id+"F19.wireOp",EDGE,"E132"),sQuery(id+"F19.wireOp",EDGE,"E133")])]});
            var Q1;
            Q1=makeQuery(id+"F1.opRevolve","SWEPT_EDGE",EDGE,{"disambiguationData":[OSD([sQuery(id+"F0.wireOp",EDGE,"E67"),sQuery(id+"F0.wireOp",EDGE,"E68")])]});
            circularPattern(context, id + "F21", {"operationType" : NewBodyOperationType.ADD, "entities" : qUnion([Q0]), "axis" : qUnion([Q1]), "angle" : 30 * degree, "instanceCount" : 16});
        }
        {
            var Q0;
            Q0=qCreatedBy(makeId("Top.planeOp"),FACE);
            var sketch = newSketch(context, id + "F22", { "sketchPlane" : qUnion([Q0])});
            skLineSegment(sketch, "E134", {"start": v(0, 0) * mm, "end": v(0, 102.87) * mm, "construction": true});
            skCircle(sketch, "E135", {"center": v(0, 102.87) * mm, "radius": 5.4 * mm});
            skSolve(sketch);
        }
        {
            var Q0;
            Q0=qSketchRegion(id+"F22",true);
            extrude(context, id + "F23", {"entities" : qUnion([Q0]), "operationType" : NewBodyOperationType.ADD, "depth" : 26.67 * mm});
        }
        {
            var Q0;
            Q0=makeQuery(id+"F23.opExtrude","CAP_FACE",FACE,{"disambiguationData":[OSD([sQuery(id+"F22.wireOp",EDGE,"E135")])],"isStart":false});
            var sketch = newSketch(context, id + "F24", { "sketchPlane" : qUnion([Q0])});
            skCircle(sketch, "E136.cCircle", {"center": v(0, 102.87) * mm, "radius": 3.5 * mm, "construction": true});
            skLineSegment(sketch, "E136.0", {"start": v(3.5, 104.89) * mm, "end": v(3.5, 100.85) * mm});
            skLineSegment(sketch, "E136.1", {"start": v(3.5, 100.85) * mm, "end": v(0, 98.84) * mm});
            skLineSegment(sketch, "E136.2", {"start": v(0, 98.84) * mm, "end": v(-3.5, 100.85) * mm});
            skLineSegment(sketch, "E136.3", {"start": v(-3.5, 100.85) * mm, "end": v(-3.5, 104.89) * mm});
            skLineSegment(sketch, "E136.4", {"start": v(-3.5, 104.89) * mm, "end": v(0, 106.9) * mm});
            skLineSegment(sketch, "E136.5", {"start": v(0, 106.9) * mm, "end": v(3.5, 104.89) * mm});
            skPoint(sketch, "E136.0.midPoint", {"position": v(3.5, 102.87) * mm});
            skSolve(sketch);
        }
        {
            var Q0;
            Q0=qSketchRegion(id+"F24",true);
            extrude(context, id + "F25", {"entities" : qUnion([Q0]), "operationType" : NewBodyOperationType.ADD, "depth" : 1.27 * mm});
        }
        {
            var Q0;
            Q0=makeQuery(id+"F1.opRevolve","SWEPT_FACE",FACE,{"disambiguationData":[OSD([sQuery(id+"F0.wireOp",EDGE,"E20.right")])]});
            var sketch = newSketch(context, id + "F26", { "sketchPlane" : qUnion([Q0])});
            skLineSegment(sketch, "E137", {"start": v(0, 6.6) * mm, "end": v(0, 17.15) * mm});
            skCircle(sketch, "E138", {"center": v(0, 11.87) * mm, "radius": 2.22 * mm});
            skCircle(sketch, "E139.1.0", {"center": v(-8.4, 8.4) * mm, "radius": 2.22 * mm});
            skCircle(sketch, "E139.2.0", {"center": v(-11.87, 0) * mm, "radius": 2.22 * mm});
            skCircle(sketch, "E139.3.0", {"center": v(-8.4, -8.4) * mm, "radius": 2.22 * mm});
            skCircle(sketch, "E139.4.0", {"center": v(0, -11.87) * mm, "radius": 2.22 * mm});
            skCircle(sketch, "E139.5.0", {"center": v(8.4, -8.4) * mm, "radius": 2.22 * mm});
            skCircle(sketch, "E139.6.0", {"center": v(11.87, 0) * mm, "radius": 2.22 * mm});
            skCircle(sketch, "E139.7.0", {"center": v(8.4, 8.4) * mm, "radius": 2.22 * mm});
            skPoint(sketch, "E139.center", {"position": v(0, 0) * mm});
            skSolve(sketch);
        }
        {
            var Q0;
            Q0=qSketchRegion(id+"F26",true);
            extrude(context, id + "F27", {"entities" : qUnion([Q0]), "operationType" : NewBodyOperationType.REMOVE, "oppositeDirection" : true, "depth" : 2.54 * mm});
        }
        {
            var Q0;
            Q0=qCreatedBy(makeId("Front.planeOp"),FACE);
            cPlane(context, id + "F28", {"entities" : qUnion([Q0]), "cplaneType" : CPlaneType.OFFSET, "offset" : 12.7 * mm, "oppositeDirection" : true, "width" : 152.4 * mm, "height" : 152.4 * mm});
        }
        {
            var Q0;
            Q0=qCreatedBy(id+"F28.planeOp",FACE);
            var sketch = newSketch(context, id + "F29", { "sketchPlane" : qUnion([Q0])});
            skArc(sketch, "E140", {"start": v(-13.48, 19.25) * mm, "mid": v(-16.61, 16.61) * mm, "end": v(-19.25, 13.48) * mm});
            skArc(sketch, "E141", {"start": v(-16.43, 23.47) * mm, "mid": v(-20.26, 20.26) * mm, "end": v(-23.47, 16.43) * mm});
            skLineSegment(sketch, "E142", {"start": v(0, 0) * mm, "end": v(0, 28.65) * mm, "construction": true});
            skLineSegment(sketch, "E143", {"start": v(4.97, 28.21) * mm, "end": v(4.08, 23.14) * mm});
            skLineSegment(sketch, "E144", {"start": v(-4.08, 23.14) * mm, "end": v(-4.97, 28.21) * mm});
            skLineSegment(sketch, "E145.1.0", {"start": v(-19.25, 13.48) * mm, "end": v(-23.47, 16.43) * mm});
            skLineSegment(sketch, "E145.1.1", {"start": v(-16.43, 23.47) * mm, "end": v(-13.48, 19.25) * mm});
            skLineSegment(sketch, "E145.2.0", {"start": v(-23.14, -4.08) * mm, "end": v(-28.21, -4.97) * mm});
            skLineSegment(sketch, "E145.2.1", {"start": v(-28.21, 4.97) * mm, "end": v(-23.14, 4.08) * mm});
            skLineSegment(sketch, "E145.3.0", {"start": v(-13.48, -19.25) * mm, "end": v(-16.43, -23.47) * mm});
            skLineSegment(sketch, "E145.3.1", {"start": v(-23.47, -16.43) * mm, "end": v(-19.25, -13.48) * mm});
            skLineSegment(sketch, "E145.4.0", {"start": v(4.08, -23.14) * mm, "end": v(4.97, -28.21) * mm});
            skLineSegment(sketch, "E145.4.1", {"start": v(-4.97, -28.21) * mm, "end": v(-4.08, -23.14) * mm});
            skLineSegment(sketch, "E145.5.0", {"start": v(19.25, -13.48) * mm, "end": v(23.47, -16.43) * mm});
            skLineSegment(sketch, "E145.5.1", {"start": v(16.43, -23.47) * mm, "end": v(13.48, -19.25) * mm});
            skLineSegment(sketch, "E145.6.0", {"start": v(23.14, 4.08) * mm, "end": v(28.21, 4.97) * mm});
            skLineSegment(sketch, "E145.6.1", {"start": v(28.21, -4.97) * mm, "end": v(23.14, -4.08) * mm});
            skLineSegment(sketch, "E145.7.0", {"start": v(13.48, 19.25) * mm, "end": v(16.43, 23.47) * mm});
            skLineSegment(sketch, "E145.7.1", {"start": v(23.47, 16.43) * mm, "end": v(19.25, 13.48) * mm});
            skArc(sketch, "E146.trimOffspring", {"start": v(4.97, 28.21) * mm, "mid": v(0, 28.65) * mm, "end": v(-4.97, 28.21) * mm});
            skArc(sketch, "E147.trimOffspring", {"start": v(4.08, 23.14) * mm, "mid": v(0, 23.5) * mm, "end": v(-4.08, 23.14) * mm});
            skArc(sketch, "E148.trimOffspring", {"start": v(23.47, 16.43) * mm, "mid": v(20.26, 20.26) * mm, "end": v(16.43, 23.47) * mm});
            skArc(sketch, "E149.trimOffspring", {"start": v(19.25, 13.48) * mm, "mid": v(16.61, 16.61) * mm, "end": v(13.48, 19.25) * mm});
            skArc(sketch, "E150.trimOffspring", {"start": v(28.21, -4.97) * mm, "mid": v(28.65, 0) * mm, "end": v(28.21, 4.97) * mm});
            skArc(sketch, "E151.trimOffspring", {"start": v(23.14, -4.08) * mm, "mid": v(23.5, 0) * mm, "end": v(23.14, 4.08) * mm});
            skArc(sketch, "E152.trimOffspring", {"start": v(16.43, -23.47) * mm, "mid": v(20.26, -20.26) * mm, "end": v(23.47, -16.43) * mm});
            skArc(sketch, "E153.trimOffspring", {"start": v(13.48, -19.25) * mm, "mid": v(16.61, -16.61) * mm, "end": v(19.25, -13.48) * mm});
            skArc(sketch, "E154.trimOffspring", {"start": v(-4.97, -28.21) * mm, "mid": v(0, -28.65) * mm, "end": v(4.97, -28.21) * mm});
            skArc(sketch, "E155.trimOffspring", {"start": v(-4.08, -23.14) * mm, "mid": v(0, -23.5) * mm, "end": v(4.08, -23.14) * mm});
            skArc(sketch, "E156.trimOffspring", {"start": v(-23.47, -16.43) * mm, "mid": v(-20.26, -20.26) * mm, "end": v(-16.43, -23.47) * mm});
            skArc(sketch, "E157.trimOffspring", {"start": v(-19.25, -13.48) * mm, "mid": v(-16.61, -16.61) * mm, "end": v(-13.48, -19.25) * mm});
            skArc(sketch, "E158.trimOffspring", {"start": v(-28.21, 4.97) * mm, "mid": v(-28.65, 0) * mm, "end": v(-28.21, -4.97) * mm});
            skArc(sketch, "E159.trimOffspring", {"start": v(-23.14, 4.08) * mm, "mid": v(-23.5, 0) * mm, "end": v(-23.14, -4.08) * mm});
            skSolve(sketch);
        }
        {
            var Q0;
            Q0=qSketchRegion(id+"F29",true);
            extrude(context, id + "F30", {"entities" : qUnion([Q0]), "operationType" : NewBodyOperationType.REMOVE, "oppositeDirection" : true, "depth" : 1.9 * mm, "hasSecondDirection" : true, "secondDirectionOppositeDirection" : false, "secondDirectionDepth" : 1.9 * mm});
        }
        {
            var Q0;
            Q0=makeQuery(id+"F1.opRevolve","SWEPT_FACE",FACE,{"disambiguationData":[OSD([sQuery(id+"F0.wireOp",EDGE,"E71")])]});
            var sketch = newSketch(context, id + "F31", { "sketchPlane" : qUnion([Q0])});
            skLineSegment(sketch, "E160", {"start": v(0, 0) * mm, "end": v(0, 27.02) * mm, "construction": true});
            skCircle(sketch, "E161", {"center": v(0, 28.93) * mm, "radius": 3.18 * mm});
            skCircle(sketch, "E162.1.0", {"center": v(-8.94, 27.51) * mm, "radius": 3.18 * mm});
            skCircle(sketch, "E162.2.0", {"center": v(-17, 23.4) * mm, "radius": 3.18 * mm});
            skCircle(sketch, "E162.3.0", {"center": v(-23.4, 17) * mm, "radius": 3.18 * mm});
            skCircle(sketch, "E162.4.0", {"center": v(-27.51, 8.94) * mm, "radius": 3.18 * mm});
            skCircle(sketch, "E162.5.0", {"center": v(-28.93, 0) * mm, "radius": 3.18 * mm});
            skCircle(sketch, "E162.6.0", {"center": v(-27.51, -8.94) * mm, "radius": 3.18 * mm});
            skCircle(sketch, "E162.7.0", {"center": v(-23.4, -17) * mm, "radius": 3.17 * mm});
            skCircle(sketch, "E162.8.0", {"center": v(-17, -23.4) * mm, "radius": 3.18 * mm});
            skCircle(sketch, "E162.9.0", {"center": v(-8.94, -27.51) * mm, "radius": 3.18 * mm});
            skCircle(sketch, "E162.10.0", {"center": v(0, -28.93) * mm, "radius": 3.18 * mm});
            skCircle(sketch, "E162.11.0", {"center": v(8.94, -27.51) * mm, "radius": 3.18 * mm});
            skCircle(sketch, "E162.12.0", {"center": v(17, -23.4) * mm, "radius": 3.18 * mm});
            skCircle(sketch, "E162.13.0", {"center": v(23.4, -17) * mm, "radius": 3.18 * mm});
            skCircle(sketch, "E162.14.0", {"center": v(27.51, -8.94) * mm, "radius": 3.18 * mm});
            skCircle(sketch, "E162.15.0", {"center": v(28.93, 0) * mm, "radius": 3.18 * mm});
            skCircle(sketch, "E162.16.0", {"center": v(27.51, 8.94) * mm, "radius": 3.18 * mm});
            skCircle(sketch, "E162.17.0", {"center": v(23.4, 17) * mm, "radius": 3.18 * mm});
            skCircle(sketch, "E162.18.0", {"center": v(17, 23.4) * mm, "radius": 3.18 * mm});
            skCircle(sketch, "E162.19.0", {"center": v(8.94, 27.51) * mm, "radius": 3.18 * mm});
            skPoint(sketch, "E162.center", {"position": v(0, 0) * mm});
            skSolve(sketch);
        }
        {
            var Q0;
            Q0=qSketchRegion(id+"F31",true);
            extrude(context, id + "F32", {"entities" : qUnion([Q0]), "operationType" : NewBodyOperationType.REMOVE, "oppositeDirection" : true, "depth" : 5.08 * mm});
        }
        {
            var Q0;
            Q0=makeQuery(id+"F1.opRevolve","SWEPT_FACE",FACE,{"disambiguationData":[OSD([sQuery(id+"F0.wireOp",EDGE,"E23.trimOffspring")])]});
            var sketch = newSketch(context, id + "F33", { "sketchPlane" : qUnion([Q0])});
            skArc(sketch, "E163", {"start": v(-4.95, 17.26) * mm, "mid": v(-5.55, 17.08) * mm, "end": v(-6.14, 16.87) * mm});
            skArc(sketch, "E164", {"start": v(-5.43, 18.92) * mm, "mid": v(-6.08, 18.72) * mm, "end": v(-6.73, 18.5) * mm});
            skLineSegment(sketch, "E165", {"start": v(0, 0) * mm, "end": v(0, 19.69) * mm, "construction": true});
            skLineSegment(sketch, "E166", {"start": v(-0.69, 19.67) * mm, "end": v(-0.63, 17.94) * mm});
            skLineSegment(sketch, "E167", {"start": v(0.63, 17.94) * mm, "end": v(0.69, 19.67) * mm});
            skLineSegment(sketch, "E168.1.0", {"start": v(-6.73, 18.5) * mm, "end": v(-6.14, 16.87) * mm});
            skLineSegment(sketch, "E168.1.1", {"start": v(-4.95, 17.26) * mm, "end": v(-5.43, 18.92) * mm});
            skLineSegment(sketch, "E168.2.0", {"start": v(-12.12, 15.51) * mm, "end": v(-11.05, 14.15) * mm});
            skLineSegment(sketch, "E168.2.1", {"start": v(-10.04, 14.89) * mm, "end": v(-11, 16.32) * mm});
            skLineSegment(sketch, "E168.3.0", {"start": v(-16.32, 11) * mm, "end": v(-14.89, 10.04) * mm});
            skLineSegment(sketch, "E168.3.1", {"start": v(-14.15, 11.05) * mm, "end": v(-15.51, 12.12) * mm});
            skLineSegment(sketch, "E168.4.0", {"start": v(-18.92, 5.43) * mm, "end": v(-17.26, 4.95) * mm});
            skLineSegment(sketch, "E168.4.1", {"start": v(-16.87, 6.14) * mm, "end": v(-18.5, 6.73) * mm});
            skLineSegment(sketch, "E168.5.0", {"start": v(-19.67, -0.69) * mm, "end": v(-17.94, -0.63) * mm});
            skLineSegment(sketch, "E168.5.1", {"start": v(-17.94, 0.63) * mm, "end": v(-19.67, 0.69) * mm});
            skLineSegment(sketch, "E168.6.0", {"start": v(-18.5, -6.73) * mm, "end": v(-16.87, -6.14) * mm});
            skLineSegment(sketch, "E168.6.1", {"start": v(-17.26, -4.95) * mm, "end": v(-18.92, -5.43) * mm});
            skLineSegment(sketch, "E168.7.0", {"start": v(-15.51, -12.12) * mm, "end": v(-14.15, -11.05) * mm});
            skLineSegment(sketch, "E168.7.1", {"start": v(-14.89, -10.04) * mm, "end": v(-16.32, -11) * mm});
            skLineSegment(sketch, "E168.8.0", {"start": v(-11, -16.32) * mm, "end": v(-10.04, -14.89) * mm});
            skLineSegment(sketch, "E168.8.1", {"start": v(-11.05, -14.15) * mm, "end": v(-12.12, -15.51) * mm});
            skLineSegment(sketch, "E168.9.0", {"start": v(-5.43, -18.92) * mm, "end": v(-4.95, -17.26) * mm});
            skLineSegment(sketch, "E168.9.1", {"start": v(-6.14, -16.87) * mm, "end": v(-6.73, -18.5) * mm});
            skLineSegment(sketch, "E168.10.0", {"start": v(0.69, -19.67) * mm, "end": v(0.63, -17.94) * mm});
            skLineSegment(sketch, "E168.10.1", {"start": v(-0.63, -17.94) * mm, "end": v(-0.69, -19.67) * mm});
            skLineSegment(sketch, "E168.11.0", {"start": v(6.73, -18.5) * mm, "end": v(6.14, -16.87) * mm});
            skLineSegment(sketch, "E168.11.1", {"start": v(4.95, -17.26) * mm, "end": v(5.43, -18.92) * mm});
            skLineSegment(sketch, "E168.12.0", {"start": v(12.12, -15.51) * mm, "end": v(11.05, -14.15) * mm});
            skLineSegment(sketch, "E168.12.1", {"start": v(10.04, -14.89) * mm, "end": v(11, -16.32) * mm});
            skLineSegment(sketch, "E168.13.0", {"start": v(16.32, -11) * mm, "end": v(14.89, -10.04) * mm});
            skLineSegment(sketch, "E168.13.1", {"start": v(14.15, -11.05) * mm, "end": v(15.51, -12.12) * mm});
            skLineSegment(sketch, "E168.14.0", {"start": v(18.92, -5.43) * mm, "end": v(17.26, -4.95) * mm});
            skLineSegment(sketch, "E168.14.1", {"start": v(16.87, -6.14) * mm, "end": v(18.5, -6.73) * mm});
            skLineSegment(sketch, "E168.15.0", {"start": v(19.67, 0.69) * mm, "end": v(17.94, 0.63) * mm});
            skLineSegment(sketch, "E168.15.1", {"start": v(17.94, -0.63) * mm, "end": v(19.67, -0.69) * mm});
            skLineSegment(sketch, "E168.16.0", {"start": v(18.5, 6.73) * mm, "end": v(16.87, 6.14) * mm});
            skLineSegment(sketch, "E168.16.1", {"start": v(17.26, 4.95) * mm, "end": v(18.92, 5.43) * mm});
            skLineSegment(sketch, "E168.17.0", {"start": v(15.51, 12.12) * mm, "end": v(14.15, 11.05) * mm});
            skLineSegment(sketch, "E168.17.1", {"start": v(14.89, 10.04) * mm, "end": v(16.32, 11) * mm});
            skLineSegment(sketch, "E168.18.0", {"start": v(11, 16.32) * mm, "end": v(10.04, 14.89) * mm});
            skLineSegment(sketch, "E168.18.1", {"start": v(11.05, 14.15) * mm, "end": v(12.12, 15.51) * mm});
            skLineSegment(sketch, "E168.19.0", {"start": v(5.43, 18.92) * mm, "end": v(4.95, 17.26) * mm});
            skLineSegment(sketch, "E168.19.1", {"start": v(6.14, 16.87) * mm, "end": v(6.73, 18.5) * mm});
            skArc(sketch, "E169.trimOffspring", {"start": v(0.69, 19.67) * mm, "mid": v(0, 19.69) * mm, "end": v(-0.69, 19.67) * mm});
            skArc(sketch, "E170.trimOffspring", {"start": v(0.63, 17.94) * mm, "mid": v(0, 17.96) * mm, "end": v(-0.63, 17.94) * mm});
            skArc(sketch, "E171.trimOffspring", {"start": v(6.73, 18.5) * mm, "mid": v(6.08, 18.72) * mm, "end": v(5.43, 18.92) * mm});
            skArc(sketch, "E172.trimOffspring", {"start": v(6.14, 16.87) * mm, "mid": v(5.55, 17.08) * mm, "end": v(4.95, 17.26) * mm});
            skArc(sketch, "E173.trimOffspring", {"start": v(12.12, 15.51) * mm, "mid": v(11.57, 15.93) * mm, "end": v(11, 16.32) * mm});
            skArc(sketch, "E174.trimOffspring", {"start": v(11.05, 14.15) * mm, "mid": v(10.55, 14.53) * mm, "end": v(10.04, 14.89) * mm});
            skArc(sketch, "E175.trimOffspring", {"start": v(16.32, 11) * mm, "mid": v(15.93, 11.57) * mm, "end": v(15.51, 12.12) * mm});
            skArc(sketch, "E176.trimOffspring", {"start": v(14.89, 10.04) * mm, "mid": v(14.53, 10.55) * mm, "end": v(14.15, 11.05) * mm});
            skArc(sketch, "E177.trimOffspring", {"start": v(18.92, 5.43) * mm, "mid": v(18.72, 6.08) * mm, "end": v(18.5, 6.73) * mm});
            skArc(sketch, "E178.trimOffspring", {"start": v(17.26, 4.95) * mm, "mid": v(17.08, 5.55) * mm, "end": v(16.87, 6.14) * mm});
            skArc(sketch, "E179.trimOffspring", {"start": v(19.67, -0.69) * mm, "mid": v(19.69, 0) * mm, "end": v(19.67, 0.69) * mm});
            skArc(sketch, "E180.trimOffspring", {"start": v(17.94, -0.63) * mm, "mid": v(17.96, 0) * mm, "end": v(17.94, 0.63) * mm});
            skArc(sketch, "E181.trimOffspring", {"start": v(18.5, -6.73) * mm, "mid": v(18.72, -6.08) * mm, "end": v(18.92, -5.43) * mm});
            skArc(sketch, "E182.trimOffspring", {"start": v(16.87, -6.14) * mm, "mid": v(17.08, -5.55) * mm, "end": v(17.26, -4.95) * mm});
            skArc(sketch, "E183.trimOffspring", {"start": v(15.51, -12.12) * mm, "mid": v(15.93, -11.57) * mm, "end": v(16.32, -11) * mm});
            skArc(sketch, "E184.trimOffspring", {"start": v(14.15, -11.05) * mm, "mid": v(14.53, -10.55) * mm, "end": v(14.89, -10.04) * mm});
            skArc(sketch, "E185.trimOffspring", {"start": v(11, -16.32) * mm, "mid": v(11.57, -15.93) * mm, "end": v(12.12, -15.51) * mm});
            skArc(sketch, "E186.trimOffspring", {"start": v(10.04, -14.89) * mm, "mid": v(10.55, -14.53) * mm, "end": v(11.05, -14.15) * mm});
            skArc(sketch, "E187.trimOffspring", {"start": v(5.43, -18.92) * mm, "mid": v(6.08, -18.72) * mm, "end": v(6.73, -18.5) * mm});
            skArc(sketch, "E188.trimOffspring", {"start": v(4.95, -17.26) * mm, "mid": v(5.55, -17.08) * mm, "end": v(6.14, -16.87) * mm});
            skArc(sketch, "E189.trimOffspring", {"start": v(-0.69, -19.67) * mm, "mid": v(0, -19.69) * mm, "end": v(0.69, -19.67) * mm});
            skArc(sketch, "E190.trimOffspring", {"start": v(-0.63, -17.94) * mm, "mid": v(0, -17.96) * mm, "end": v(0.63, -17.94) * mm});
            skArc(sketch, "E191.trimOffspring", {"start": v(-6.73, -18.5) * mm, "mid": v(-6.08, -18.72) * mm, "end": v(-5.43, -18.92) * mm});
            skArc(sketch, "E192.trimOffspring", {"start": v(-6.14, -16.87) * mm, "mid": v(-5.55, -17.08) * mm, "end": v(-4.95, -17.26) * mm});
            skArc(sketch, "E193.trimOffspring", {"start": v(-12.12, -15.51) * mm, "mid": v(-11.57, -15.93) * mm, "end": v(-11, -16.32) * mm});
            skArc(sketch, "E194.trimOffspring", {"start": v(-11.05, -14.15) * mm, "mid": v(-10.55, -14.53) * mm, "end": v(-10.04, -14.89) * mm});
            skArc(sketch, "E195.trimOffspring", {"start": v(-16.32, -11) * mm, "mid": v(-15.93, -11.57) * mm, "end": v(-15.51, -12.12) * mm});
            skArc(sketch, "E196.trimOffspring", {"start": v(-14.89, -10.04) * mm, "mid": v(-14.53, -10.55) * mm, "end": v(-14.15, -11.05) * mm});
            skArc(sketch, "E197.trimOffspring", {"start": v(-18.92, -5.43) * mm, "mid": v(-18.72, -6.08) * mm, "end": v(-18.5, -6.73) * mm});
            skArc(sketch, "E198.trimOffspring", {"start": v(-17.26, -4.95) * mm, "mid": v(-17.08, -5.55) * mm, "end": v(-16.87, -6.14) * mm});
            skArc(sketch, "E199.trimOffspring", {"start": v(-19.67, 0.69) * mm, "mid": v(-19.69, 0) * mm, "end": v(-19.67, -0.69) * mm});
            skArc(sketch, "E200.trimOffspring", {"start": v(-17.94, 0.63) * mm, "mid": v(-17.96, 0) * mm, "end": v(-17.94, -0.63) * mm});
            skArc(sketch, "E201.trimOffspring", {"start": v(-18.5, 6.73) * mm, "mid": v(-18.72, 6.08) * mm, "end": v(-18.92, 5.43) * mm});
            skArc(sketch, "E202.trimOffspring", {"start": v(-16.87, 6.14) * mm, "mid": v(-17.08, 5.55) * mm, "end": v(-17.26, 4.95) * mm});
            skArc(sketch, "E203.trimOffspring", {"start": v(-15.51, 12.12) * mm, "mid": v(-15.93, 11.57) * mm, "end": v(-16.32, 11) * mm});
            skArc(sketch, "E204.trimOffspring", {"start": v(-14.15, 11.05) * mm, "mid": v(-14.53, 10.55) * mm, "end": v(-14.89, 10.04) * mm});
            skArc(sketch, "E205.trimOffspring", {"start": v(-11, 16.32) * mm, "mid": v(-11.57, 15.93) * mm, "end": v(-12.12, 15.51) * mm});
            skArc(sketch, "E206.trimOffspring", {"start": v(-10.04, 14.89) * mm, "mid": v(-10.55, 14.53) * mm, "end": v(-11.05, 14.15) * mm});
            skSolve(sketch);
        }
        {
            var Q0;
            Q0=qSketchRegion(id+"F33",true);
            extrude(context, id + "F34", {"entities" : qUnion([Q0]), "operationType" : NewBodyOperationType.REMOVE, "depth" : 25.4 * mm});
        }
        {
            var Q0;
            Q0=makeQuery(id+"F30.boolean.opBoolean","COPY",EDGE,{"derivedFrom":makeQuery(id+"F30.opExtrude","CAP_EDGE",EDGE,{"disambiguationData":[OSD([sQuery(id+"F29.wireOp",EDGE,"E145.7.0")])],"isStart":false})});
            var Q1;
            Q1=makeQuery(id+"F30.boolean.opBoolean","COPY",EDGE,{"derivedFrom":makeQuery(id+"F30.opExtrude","CAP_EDGE",EDGE,{"disambiguationData":[OSD([sQuery(id+"F29.wireOp",EDGE,"E145.7.0")])],"isStart":true})});
            var Q2;
            Q2=makeQuery(id+"F30.boolean.opBoolean","COPY",EDGE,{"derivedFrom":makeQuery(id+"F30.opExtrude","CAP_EDGE",EDGE,{"disambiguationData":[OSD([sQuery(id+"F29.wireOp",EDGE,"E144")])],"isStart":true})});
            var Q3;
            Q3=makeQuery(id+"F30.boolean.opBoolean","COPY",EDGE,{"derivedFrom":makeQuery(id+"F30.opExtrude","CAP_EDGE",EDGE,{"disambiguationData":[OSD([sQuery(id+"F29.wireOp",EDGE,"E144")])],"isStart":false})});
            var Q4;
            Q4=makeQuery(id+"F30.boolean.opBoolean","COPY",EDGE,{"derivedFrom":makeQuery(id+"F30.opExtrude","CAP_EDGE",EDGE,{"disambiguationData":[OSD([sQuery(id+"F29.wireOp",EDGE,"E145.7.1")])],"isStart":true})});
            var Q5;
            Q5=makeQuery(id+"F30.boolean.opBoolean","COPY",EDGE,{"derivedFrom":makeQuery(id+"F30.opExtrude","CAP_EDGE",EDGE,{"disambiguationData":[OSD([sQuery(id+"F29.wireOp",EDGE,"E143")])],"isStart":true})});
            var Q6;
            Q6=makeQuery(id+"F30.boolean.opBoolean","COPY",EDGE,{"derivedFrom":makeQuery(id+"F30.opExtrude","CAP_EDGE",EDGE,{"disambiguationData":[OSD([sQuery(id+"F29.wireOp",EDGE,"E145.7.1")])],"isStart":false})});
            var Q7;
            Q7=makeQuery(id+"F30.boolean.opBoolean","COPY",EDGE,{"derivedFrom":makeQuery(id+"F30.opExtrude","CAP_EDGE",EDGE,{"disambiguationData":[OSD([sQuery(id+"F29.wireOp",EDGE,"E143")])],"isStart":false})});
            var Q8;
            Q8=makeQuery(id+"F30.boolean.opBoolean","COPY",EDGE,{"derivedFrom":makeQuery(id+"F30.opExtrude","CAP_EDGE",EDGE,{"disambiguationData":[OSD([sQuery(id+"F29.wireOp",EDGE,"E145.6.1")])],"isStart":false})});
            var Q9;
            Q9=makeQuery(id+"F30.boolean.opBoolean","COPY",EDGE,{"derivedFrom":makeQuery(id+"F30.opExtrude","CAP_EDGE",EDGE,{"disambiguationData":[OSD([sQuery(id+"F29.wireOp",EDGE,"E145.6.1")])],"isStart":true})});
            var Q10;
            Q10=makeQuery(id+"F30.boolean.opBoolean","COPY",EDGE,{"derivedFrom":makeQuery(id+"F30.opExtrude","CAP_EDGE",EDGE,{"disambiguationData":[OSD([sQuery(id+"F29.wireOp",EDGE,"E145.6.0")])],"isStart":true})});
            var Q11;
            Q11=makeQuery(id+"F30.boolean.opBoolean","COPY",EDGE,{"derivedFrom":makeQuery(id+"F30.opExtrude","CAP_EDGE",EDGE,{"disambiguationData":[OSD([sQuery(id+"F29.wireOp",EDGE,"E145.6.0")])],"isStart":false})});
            var Q12;
            Q12=makeQuery(id+"F30.boolean.opBoolean","COPY",EDGE,{"derivedFrom":makeQuery(id+"F30.opExtrude","CAP_EDGE",EDGE,{"disambiguationData":[OSD([sQuery(id+"F29.wireOp",EDGE,"E145.5.1")])],"isStart":false})});
            var Q13;
            Q13=makeQuery(id+"F30.boolean.opBoolean","COPY",EDGE,{"derivedFrom":makeQuery(id+"F30.opExtrude","CAP_EDGE",EDGE,{"disambiguationData":[OSD([sQuery(id+"F29.wireOp",EDGE,"E145.5.0")])],"isStart":false})});
            var Q14;
            Q14=makeQuery(id+"F30.boolean.opBoolean","COPY",EDGE,{"derivedFrom":makeQuery(id+"F30.opExtrude","CAP_EDGE",EDGE,{"disambiguationData":[OSD([sQuery(id+"F29.wireOp",EDGE,"E145.5.1")])],"isStart":true})});
            var Q15;
            Q15=makeQuery(id+"F30.boolean.opBoolean","COPY",EDGE,{"derivedFrom":makeQuery(id+"F30.opExtrude","CAP_EDGE",EDGE,{"disambiguationData":[OSD([sQuery(id+"F29.wireOp",EDGE,"E145.5.0")])],"isStart":true})});
            var Q16;
            Q16=makeQuery(id+"F30.boolean.opBoolean","COPY",EDGE,{"derivedFrom":makeQuery(id+"F30.opExtrude","CAP_EDGE",EDGE,{"disambiguationData":[OSD([sQuery(id+"F29.wireOp",EDGE,"E145.4.1")])],"isStart":true})});
            var Q17;
            Q17=makeQuery(id+"F30.boolean.opBoolean","COPY",EDGE,{"derivedFrom":makeQuery(id+"F30.opExtrude","CAP_EDGE",EDGE,{"disambiguationData":[OSD([sQuery(id+"F29.wireOp",EDGE,"E145.4.0")])],"isStart":true})});
            var Q18;
            Q18=makeQuery(id+"F30.boolean.opBoolean","COPY",EDGE,{"derivedFrom":makeQuery(id+"F30.opExtrude","CAP_EDGE",EDGE,{"disambiguationData":[OSD([sQuery(id+"F29.wireOp",EDGE,"E145.4.1")])],"isStart":false})});
            var Q19;
            Q19=makeQuery(id+"F30.boolean.opBoolean","COPY",EDGE,{"derivedFrom":makeQuery(id+"F30.opExtrude","CAP_EDGE",EDGE,{"disambiguationData":[OSD([sQuery(id+"F29.wireOp",EDGE,"E145.4.0")])],"isStart":false})});
            var Q20;
            Q20=makeQuery(id+"F30.boolean.opBoolean","COPY",EDGE,{"derivedFrom":makeQuery(id+"F30.opExtrude","CAP_EDGE",EDGE,{"disambiguationData":[OSD([sQuery(id+"F29.wireOp",EDGE,"E145.3.0")])],"isStart":false})});
            var Q21;
            Q21=makeQuery(id+"F30.boolean.opBoolean","COPY",EDGE,{"derivedFrom":makeQuery(id+"F30.opExtrude","CAP_EDGE",EDGE,{"disambiguationData":[OSD([sQuery(id+"F29.wireOp",EDGE,"E145.3.1")])],"isStart":false})});
            var Q22;
            Q22=makeQuery(id+"F30.boolean.opBoolean","COPY",EDGE,{"derivedFrom":makeQuery(id+"F30.opExtrude","CAP_EDGE",EDGE,{"disambiguationData":[OSD([sQuery(id+"F29.wireOp",EDGE,"E145.3.1")])],"isStart":true})});
            var Q23;
            Q23=makeQuery(id+"F30.boolean.opBoolean","COPY",EDGE,{"derivedFrom":makeQuery(id+"F30.opExtrude","CAP_EDGE",EDGE,{"disambiguationData":[OSD([sQuery(id+"F29.wireOp",EDGE,"E145.3.0")])],"isStart":true})});
            var Q24;
            Q24=makeQuery(id+"F30.boolean.opBoolean","COPY",EDGE,{"derivedFrom":makeQuery(id+"F30.opExtrude","CAP_EDGE",EDGE,{"disambiguationData":[OSD([sQuery(id+"F29.wireOp",EDGE,"E145.2.1")])],"isStart":false})});
            var Q25;
            Q25=makeQuery(id+"F30.boolean.opBoolean","COPY",EDGE,{"derivedFrom":makeQuery(id+"F30.opExtrude","CAP_EDGE",EDGE,{"disambiguationData":[OSD([sQuery(id+"F29.wireOp",EDGE,"E145.2.0")])],"isStart":false})});
            var Q26;
            Q26=makeQuery(id+"F30.boolean.opBoolean","COPY",EDGE,{"derivedFrom":makeQuery(id+"F30.opExtrude","CAP_EDGE",EDGE,{"disambiguationData":[OSD([sQuery(id+"F29.wireOp",EDGE,"E145.2.0")])],"isStart":true})});
            var Q27;
            Q27=makeQuery(id+"F30.boolean.opBoolean","COPY",EDGE,{"derivedFrom":makeQuery(id+"F30.opExtrude","CAP_EDGE",EDGE,{"disambiguationData":[OSD([sQuery(id+"F29.wireOp",EDGE,"E145.2.1")])],"isStart":true})});
            var Q28;
            Q28=makeQuery(id+"F30.boolean.opBoolean","COPY",EDGE,{"derivedFrom":makeQuery(id+"F30.opExtrude","CAP_EDGE",EDGE,{"disambiguationData":[OSD([sQuery(id+"F29.wireOp",EDGE,"E145.1.1")])],"isStart":true})});
            var Q29;
            Q29=makeQuery(id+"F30.boolean.opBoolean","COPY",EDGE,{"derivedFrom":makeQuery(id+"F30.opExtrude","CAP_EDGE",EDGE,{"disambiguationData":[OSD([sQuery(id+"F29.wireOp",EDGE,"E145.1.0")])],"isStart":true})});
            var Q30;
            Q30=makeQuery(id+"F30.boolean.opBoolean","COPY",EDGE,{"derivedFrom":makeQuery(id+"F30.opExtrude","CAP_EDGE",EDGE,{"disambiguationData":[OSD([sQuery(id+"F29.wireOp",EDGE,"E145.1.0")])],"isStart":false})});
            var Q31;
            Q31=makeQuery(id+"F30.boolean.opBoolean","COPY",EDGE,{"derivedFrom":makeQuery(id+"F30.opExtrude","CAP_EDGE",EDGE,{"disambiguationData":[OSD([sQuery(id+"F29.wireOp",EDGE,"E145.1.1")])],"isStart":false})});
            fillet(context, id + "F35", {"entities" : qUnion([Q0, Q1, Q2, Q3, Q4, Q5, Q6, Q7, Q8, Q9, Q10, Q11, Q12, Q13, Q14, Q15, Q16, Q17, Q18, Q19, Q20, Q21, Q22, Q23, Q24, Q25, Q26, Q27, Q28, Q29, Q30, Q31]), "radius" : 0.64 * mm, "tangentPropagation" : true, "allowEdgeOverflow" : false});
        }
        {
            var Q0;
            Q0=makeQuery(id+"F18.boolean.opBoolean","INTERSECT",EDGE,{"derivedFrom":[makeQuery(id+"F18.opPattern","COPY",FACE,{"derivedFrom":makeQuery(id+"F10.opSweep","SWEPT_FACE",FACE,{"disambiguationData":[OSD([sQuery(id+"F7.wireOp",EDGE,"E115"),sQuery(id+"F9.wireOp",EDGE,"E120")])]}),"instanceName":"2"}),makeQuery(id+"F18.opPattern","COPY",FACE,{"derivedFrom":makeQuery(id+"F12.opRevolve","SWEPT_FACE",FACE,{"disambiguationData":[OSD([sQuery(id+"F11.wireOp",EDGE,"E121.top")])]}),"instanceName":"2"})]});
            var Q1;
            Q1=makeQuery(id+"F18.boolean.opBoolean","INTERSECT",EDGE,{"derivedFrom":[makeQuery(id+"F18.opPattern","COPY",FACE,{"derivedFrom":makeQuery(id+"F10.opSweep","SWEPT_FACE",FACE,{"disambiguationData":[OSD([sQuery(id+"F7.wireOp",EDGE,"E115"),sQuery(id+"F9.wireOp",EDGE,"E120")])]}),"instanceName":"1"}),makeQuery(id+"F18.opPattern","COPY",FACE,{"derivedFrom":makeQuery(id+"F12.opRevolve","SWEPT_FACE",FACE,{"disambiguationData":[OSD([sQuery(id+"F11.wireOp",EDGE,"E121.top")])]}),"instanceName":"1"})]});
            var Q2;
            Q2=makeQuery(id+"F18.boolean.opBoolean","INTERSECT",EDGE,{"derivedFrom":[makeQuery(id+"F10.opSweep","SWEPT_FACE",FACE,{"disambiguationData":[OSD([sQuery(id+"F7.wireOp",EDGE,"E115"),sQuery(id+"F9.wireOp",EDGE,"E120")])]}),makeQuery(id+"F12.opRevolve","SWEPT_FACE",FACE,{"disambiguationData":[OSD([sQuery(id+"F11.wireOp",EDGE,"E121.top")])]})]});
            var Q3;
            Q3=makeQuery(id+"F18.boolean.opBoolean","INTERSECT",EDGE,{"derivedFrom":[makeQuery(id+"F18.opPattern","COPY",FACE,{"derivedFrom":makeQuery(id+"F10.opSweep","SWEPT_FACE",FACE,{"disambiguationData":[OSD([sQuery(id+"F7.wireOp",EDGE,"E115"),sQuery(id+"F9.wireOp",EDGE,"E120")])]}),"instanceName":"7"}),makeQuery(id+"F18.opPattern","COPY",FACE,{"derivedFrom":makeQuery(id+"F12.opRevolve","SWEPT_FACE",FACE,{"disambiguationData":[OSD([sQuery(id+"F11.wireOp",EDGE,"E121.top")])]}),"instanceName":"7"})]});
            var Q4;
            Q4=makeQuery(id+"F18.boolean.opBoolean","INTERSECT",EDGE,{"derivedFrom":[makeQuery(id+"F18.opPattern","COPY",FACE,{"derivedFrom":makeQuery(id+"F10.opSweep","SWEPT_FACE",FACE,{"disambiguationData":[OSD([sQuery(id+"F7.wireOp",EDGE,"E115"),sQuery(id+"F9.wireOp",EDGE,"E120")])]}),"instanceName":"6"}),makeQuery(id+"F18.opPattern","COPY",FACE,{"derivedFrom":makeQuery(id+"F12.opRevolve","SWEPT_FACE",FACE,{"disambiguationData":[OSD([sQuery(id+"F11.wireOp",EDGE,"E121.top")])]}),"instanceName":"6"})]});
            var Q5;
            Q5=makeQuery(id+"F18.boolean.opBoolean","INTERSECT",EDGE,{"derivedFrom":[makeQuery(id+"F18.opPattern","COPY",FACE,{"derivedFrom":makeQuery(id+"F10.opSweep","SWEPT_FACE",FACE,{"disambiguationData":[OSD([sQuery(id+"F7.wireOp",EDGE,"E115"),sQuery(id+"F9.wireOp",EDGE,"E120")])]}),"instanceName":"5"}),makeQuery(id+"F18.opPattern","COPY",FACE,{"derivedFrom":makeQuery(id+"F12.opRevolve","SWEPT_FACE",FACE,{"disambiguationData":[OSD([sQuery(id+"F11.wireOp",EDGE,"E121.top")])]}),"instanceName":"5"})]});
            var Q6;
            Q6=makeQuery(id+"F18.boolean.opBoolean","INTERSECT",EDGE,{"derivedFrom":[makeQuery(id+"F18.opPattern","COPY",FACE,{"derivedFrom":makeQuery(id+"F10.opSweep","SWEPT_FACE",FACE,{"disambiguationData":[OSD([sQuery(id+"F7.wireOp",EDGE,"E115"),sQuery(id+"F9.wireOp",EDGE,"E120")])]}),"instanceName":"4"}),makeQuery(id+"F18.opPattern","COPY",FACE,{"derivedFrom":makeQuery(id+"F12.opRevolve","SWEPT_FACE",FACE,{"disambiguationData":[OSD([sQuery(id+"F11.wireOp",EDGE,"E121.top")])]}),"instanceName":"4"})]});
            var Q7;
            Q7=makeQuery(id+"F18.boolean.opBoolean","INTERSECT",EDGE,{"derivedFrom":[makeQuery(id+"F18.opPattern","COPY",FACE,{"derivedFrom":makeQuery(id+"F10.opSweep","SWEPT_FACE",FACE,{"disambiguationData":[OSD([sQuery(id+"F7.wireOp",EDGE,"E115"),sQuery(id+"F9.wireOp",EDGE,"E120")])]}),"instanceName":"3"}),makeQuery(id+"F18.opPattern","COPY",FACE,{"derivedFrom":makeQuery(id+"F12.opRevolve","SWEPT_FACE",FACE,{"disambiguationData":[OSD([sQuery(id+"F11.wireOp",EDGE,"E121.top")])]}),"instanceName":"3"})]});
            fillet(context, id + "F36", {"entities" : qUnion([Q0, Q1, Q2, Q3, Q4, Q5, Q6, Q7]), "radius" : 1.27 * mm, "tangentPropagation" : true, "allowEdgeOverflow" : false});
        }
        {
            var Q0;
            Q0=makeQuery(id+"F18.boolean.opBoolean","INTERSECT",EDGE,{"derivedFrom":[makeQuery(id+"F18.opPattern","COPY",FACE,{"derivedFrom":makeQuery(id+"F10.opSweep","SWEPT_FACE",FACE,{"disambiguationData":[OSD([sQuery(id+"F7.wireOp",EDGE,"E117"),sQuery(id+"F9.wireOp",EDGE,"E120")])]}),"instanceName":"2"}),makeQuery(id+"F18.opPattern","COPY",FACE,{"derivedFrom":makeQuery(id+"F12.opRevolve","SWEPT_FACE",FACE,{"disambiguationData":[OSD([sQuery(id+"F11.wireOp",EDGE,"E122.top")])]}),"instanceName":"2"})]});
            var Q1;
            Q1=makeQuery(id+"F18.boolean.opBoolean","INTERSECT",EDGE,{"derivedFrom":[makeQuery(id+"F18.opPattern","COPY",FACE,{"derivedFrom":makeQuery(id+"F10.opSweep","SWEPT_FACE",FACE,{"disambiguationData":[OSD([sQuery(id+"F7.wireOp",EDGE,"E117"),sQuery(id+"F9.wireOp",EDGE,"E120")])]}),"instanceName":"1"}),makeQuery(id+"F18.opPattern","COPY",FACE,{"derivedFrom":makeQuery(id+"F12.opRevolve","SWEPT_FACE",FACE,{"disambiguationData":[OSD([sQuery(id+"F11.wireOp",EDGE,"E122.top")])]}),"instanceName":"1"})]});
            var Q2;
            Q2=makeQuery(id+"F18.boolean.opBoolean","INTERSECT",EDGE,{"derivedFrom":[makeQuery(id+"F10.opSweep","SWEPT_FACE",FACE,{"disambiguationData":[OSD([sQuery(id+"F7.wireOp",EDGE,"E117"),sQuery(id+"F9.wireOp",EDGE,"E120")])]}),makeQuery(id+"F12.opRevolve","SWEPT_FACE",FACE,{"disambiguationData":[OSD([sQuery(id+"F11.wireOp",EDGE,"E122.top")])]})]});
            var Q3;
            Q3=makeQuery(id+"F18.boolean.opBoolean","INTERSECT",EDGE,{"derivedFrom":[makeQuery(id+"F18.opPattern","COPY",FACE,{"derivedFrom":makeQuery(id+"F10.opSweep","SWEPT_FACE",FACE,{"disambiguationData":[OSD([sQuery(id+"F7.wireOp",EDGE,"E117"),sQuery(id+"F9.wireOp",EDGE,"E120")])]}),"instanceName":"7"}),makeQuery(id+"F18.opPattern","COPY",FACE,{"derivedFrom":makeQuery(id+"F12.opRevolve","SWEPT_FACE",FACE,{"disambiguationData":[OSD([sQuery(id+"F11.wireOp",EDGE,"E122.top")])]}),"instanceName":"7"})]});
            var Q4;
            Q4=makeQuery(id+"F18.boolean.opBoolean","INTERSECT",EDGE,{"derivedFrom":[makeQuery(id+"F18.opPattern","COPY",FACE,{"derivedFrom":makeQuery(id+"F10.opSweep","SWEPT_FACE",FACE,{"disambiguationData":[OSD([sQuery(id+"F7.wireOp",EDGE,"E117"),sQuery(id+"F9.wireOp",EDGE,"E120")])]}),"instanceName":"6"}),makeQuery(id+"F18.opPattern","COPY",FACE,{"derivedFrom":makeQuery(id+"F12.opRevolve","SWEPT_FACE",FACE,{"disambiguationData":[OSD([sQuery(id+"F11.wireOp",EDGE,"E122.top")])]}),"instanceName":"6"})]});
            var Q5;
            Q5=makeQuery(id+"F18.boolean.opBoolean","INTERSECT",EDGE,{"derivedFrom":[makeQuery(id+"F18.opPattern","COPY",FACE,{"derivedFrom":makeQuery(id+"F10.opSweep","SWEPT_FACE",FACE,{"disambiguationData":[OSD([sQuery(id+"F7.wireOp",EDGE,"E117"),sQuery(id+"F9.wireOp",EDGE,"E120")])]}),"instanceName":"5"}),makeQuery(id+"F18.opPattern","COPY",FACE,{"derivedFrom":makeQuery(id+"F12.opRevolve","SWEPT_FACE",FACE,{"disambiguationData":[OSD([sQuery(id+"F11.wireOp",EDGE,"E122.top")])]}),"instanceName":"5"})]});
            var Q6;
            Q6=makeQuery(id+"F18.boolean.opBoolean","INTERSECT",EDGE,{"derivedFrom":[makeQuery(id+"F18.opPattern","COPY",FACE,{"derivedFrom":makeQuery(id+"F10.opSweep","SWEPT_FACE",FACE,{"disambiguationData":[OSD([sQuery(id+"F7.wireOp",EDGE,"E117"),sQuery(id+"F9.wireOp",EDGE,"E120")])]}),"instanceName":"4"}),makeQuery(id+"F18.opPattern","COPY",FACE,{"derivedFrom":makeQuery(id+"F12.opRevolve","SWEPT_FACE",FACE,{"disambiguationData":[OSD([sQuery(id+"F11.wireOp",EDGE,"E122.top")])]}),"instanceName":"4"})]});
            var Q7;
            Q7=makeQuery(id+"F18.boolean.opBoolean","INTERSECT",EDGE,{"derivedFrom":[makeQuery(id+"F18.opPattern","COPY",FACE,{"derivedFrom":makeQuery(id+"F10.opSweep","SWEPT_FACE",FACE,{"disambiguationData":[OSD([sQuery(id+"F7.wireOp",EDGE,"E117"),sQuery(id+"F9.wireOp",EDGE,"E120")])]}),"instanceName":"3"}),makeQuery(id+"F18.opPattern","COPY",FACE,{"derivedFrom":makeQuery(id+"F12.opRevolve","SWEPT_FACE",FACE,{"disambiguationData":[OSD([sQuery(id+"F11.wireOp",EDGE,"E122.top")])]}),"instanceName":"3"})]});
            fillet(context, id + "F37", {"entities" : qUnion([Q0, Q1, Q2, Q3, Q4, Q5, Q6, Q7]), "radius" : 1.27 * mm, "tangentPropagation" : true, "allowEdgeOverflow" : false});
        }
        {
            var Q0;
            Q0=makeQuery(id+"F1.opRevolve","SWEPT_EDGE",EDGE,{"disambiguationData":[OSD([sQuery(id+"F0.wireOp",EDGE,"E9"),sQuery(id+"F0.wireOp",EDGE,"E60.trimOffspring")])]});
            fillet(context, id + "F38", {"entities" : qUnion([Q0]), "radius" : 6.35 * mm, "tangentPropagation" : true, "allowEdgeOverflow" : false});
        }
        {
            var Q0;
            Q0=makeQuery(id+"F1.opRevolve","SWEPT_EDGE",EDGE,{"disambiguationData":[OSD([sQuery(id+"F0.wireOp",EDGE,"E7"),sQuery(id+"F0.wireOp",EDGE,"E8")])]});
            chamfer(context, id + "F39", {"entities" : qUnion([Q0]), "width" : 0.64 * mm, "tangentPropagation" : true});
        }
        {
            var Q0;
            {var subQ0=sQuery(id+"F0.wireOp",EDGE,"E1");var subQ1=sQuery(id+"F0.wireOp",EDGE,"E67");var subQ2=sQuery(id+"F19.wireOp",EDGE,"E133");var subQ3=sQuery(id+"F19.wireOp",EDGE,"E132");var subQ4=sQuery(id+"F19.wireOp",EDGE,"E131");var subQ5=sQuery(id+"F19.wireOp",EDGE,"E130");Q0=makeQuery(id+"F21.boolean.opBoolean","SPLIT",EDGE,{"disambiguationData":[TD([makeQuery(id+"F21.opPattern","COPY",FACE,{"derivedFrom":makeQuery(id+"F20.opExtrude","CAP_FACE",FACE,{"disambiguationData":[OSD([subQ5,subQ4,subQ3,subQ2])],"isStart":true}),"instanceName":"10"})])],"derivedFrom":makeQuery(id+"F1.opRevolve","SWEPT_EDGE",EDGE,{"disambiguationData":[OSD([subQ0,subQ1])]})});}
            var Q1;
            {var subQ0=sQuery(id+"F0.wireOp",EDGE,"E1");var subQ1=sQuery(id+"F19.wireOp",EDGE,"E133");var subQ2=sQuery(id+"F19.wireOp",EDGE,"E132");var subQ3=sQuery(id+"F19.wireOp",EDGE,"E131");var subQ4=sQuery(id+"F19.wireOp",EDGE,"E130");var subQ5=sQuery(id+"F0.wireOp",EDGE,"E67");Q1=makeQuery(id+"F21.boolean.opBoolean","SPLIT",EDGE,{"disambiguationData":[TD([makeQuery(id+"F21.opPattern","COPY",FACE,{"derivedFrom":makeQuery(id+"F20.opExtrude","CAP_FACE",FACE,{"disambiguationData":[OSD([subQ4,subQ3,subQ2,subQ1])],"isStart":true}),"instanceName":"9"})])],"derivedFrom":makeQuery(id+"F1.opRevolve","SWEPT_EDGE",EDGE,{"disambiguationData":[OSD([subQ0,subQ5])]})});}
            var Q2;
            {var subQ0=sQuery(id+"F0.wireOp",EDGE,"E1");var subQ1=sQuery(id+"F0.wireOp",EDGE,"E67");var subQ2=sQuery(id+"F19.wireOp",EDGE,"E133");var subQ3=sQuery(id+"F19.wireOp",EDGE,"E132");var subQ4=sQuery(id+"F19.wireOp",EDGE,"E131");var subQ5=sQuery(id+"F19.wireOp",EDGE,"E130");Q2=makeQuery(id+"F21.boolean.opBoolean","SPLIT",EDGE,{"disambiguationData":[TD([makeQuery(id+"F21.opPattern","COPY",FACE,{"derivedFrom":makeQuery(id+"F20.opExtrude","CAP_FACE",FACE,{"disambiguationData":[OSD([subQ5,subQ4,subQ3,subQ2])],"isStart":true}),"instanceName":"8"})])],"derivedFrom":makeQuery(id+"F1.opRevolve","SWEPT_EDGE",EDGE,{"disambiguationData":[OSD([subQ0,subQ1])]})});}
            var Q3;
            {var subQ0=sQuery(id+"F0.wireOp",EDGE,"E1");var subQ1=sQuery(id+"F19.wireOp",EDGE,"E133");var subQ2=sQuery(id+"F19.wireOp",EDGE,"E132");var subQ3=sQuery(id+"F19.wireOp",EDGE,"E131");var subQ4=sQuery(id+"F19.wireOp",EDGE,"E130");var subQ5=sQuery(id+"F0.wireOp",EDGE,"E67");Q3=makeQuery(id+"F21.boolean.opBoolean","SPLIT",EDGE,{"disambiguationData":[TD([makeQuery(id+"F21.opPattern","COPY",FACE,{"derivedFrom":makeQuery(id+"F20.opExtrude","CAP_FACE",FACE,{"disambiguationData":[OSD([subQ4,subQ3,subQ2,subQ1])],"isStart":true}),"instanceName":"7"})])],"derivedFrom":makeQuery(id+"F1.opRevolve","SWEPT_EDGE",EDGE,{"disambiguationData":[OSD([subQ0,subQ5])]})});}
            var Q4;
            {var subQ0=sQuery(id+"F0.wireOp",EDGE,"E1");var subQ1=sQuery(id+"F0.wireOp",EDGE,"E67");var subQ2=sQuery(id+"F19.wireOp",EDGE,"E133");var subQ3=sQuery(id+"F19.wireOp",EDGE,"E132");var subQ4=sQuery(id+"F19.wireOp",EDGE,"E131");var subQ5=sQuery(id+"F19.wireOp",EDGE,"E130");Q4=makeQuery(id+"F21.boolean.opBoolean","SPLIT",EDGE,{"disambiguationData":[TD([makeQuery(id+"F21.opPattern","COPY",FACE,{"derivedFrom":makeQuery(id+"F20.opExtrude","CAP_FACE",FACE,{"disambiguationData":[OSD([subQ5,subQ4,subQ3,subQ2])],"isStart":true}),"instanceName":"6"})])],"derivedFrom":makeQuery(id+"F1.opRevolve","SWEPT_EDGE",EDGE,{"disambiguationData":[OSD([subQ0,subQ1])]})});}
            var Q5;
            {var subQ0=sQuery(id+"F0.wireOp",EDGE,"E1");var subQ1=sQuery(id+"F0.wireOp",EDGE,"E67");var subQ2=sQuery(id+"F19.wireOp",EDGE,"E133");var subQ3=sQuery(id+"F19.wireOp",EDGE,"E132");var subQ4=sQuery(id+"F19.wireOp",EDGE,"E131");var subQ5=sQuery(id+"F19.wireOp",EDGE,"E130");Q5=makeQuery(id+"F21.boolean.opBoolean","SPLIT",EDGE,{"disambiguationData":[TD([makeQuery(id+"F21.opPattern","COPY",FACE,{"derivedFrom":makeQuery(id+"F20.opExtrude","CAP_FACE",FACE,{"disambiguationData":[OSD([subQ5,subQ4,subQ3,subQ2])],"isStart":true}),"instanceName":"5"})])],"derivedFrom":makeQuery(id+"F1.opRevolve","SWEPT_EDGE",EDGE,{"disambiguationData":[OSD([subQ0,subQ1])]})});}
            var Q6;
            {var subQ0=sQuery(id+"F0.wireOp",EDGE,"E1");var subQ1=sQuery(id+"F0.wireOp",EDGE,"E67");var subQ2=sQuery(id+"F19.wireOp",EDGE,"E133");var subQ3=sQuery(id+"F19.wireOp",EDGE,"E132");var subQ4=sQuery(id+"F19.wireOp",EDGE,"E131");var subQ5=sQuery(id+"F19.wireOp",EDGE,"E130");Q6=makeQuery(id+"F21.boolean.opBoolean","SPLIT",EDGE,{"disambiguationData":[TD([makeQuery(id+"F21.opPattern","COPY",FACE,{"derivedFrom":makeQuery(id+"F20.opExtrude","CAP_FACE",FACE,{"disambiguationData":[OSD([subQ5,subQ4,subQ3,subQ2])],"isStart":true}),"instanceName":"4"})])],"derivedFrom":makeQuery(id+"F1.opRevolve","SWEPT_EDGE",EDGE,{"disambiguationData":[OSD([subQ0,subQ1])]})});}
            var Q7;
            {var subQ0=sQuery(id+"F0.wireOp",EDGE,"E1");var subQ1=sQuery(id+"F19.wireOp",EDGE,"E133");var subQ2=sQuery(id+"F19.wireOp",EDGE,"E132");var subQ3=sQuery(id+"F19.wireOp",EDGE,"E131");var subQ4=sQuery(id+"F19.wireOp",EDGE,"E130");var subQ5=sQuery(id+"F0.wireOp",EDGE,"E67");Q7=makeQuery(id+"F21.boolean.opBoolean","SPLIT",EDGE,{"disambiguationData":[TD([makeQuery(id+"F21.opPattern","COPY",FACE,{"derivedFrom":makeQuery(id+"F20.opExtrude","CAP_FACE",FACE,{"disambiguationData":[OSD([subQ4,subQ3,subQ2,subQ1])],"isStart":true}),"instanceName":"3"})])],"derivedFrom":makeQuery(id+"F1.opRevolve","SWEPT_EDGE",EDGE,{"disambiguationData":[OSD([subQ0,subQ5])]})});}
            var Q8;
            {var subQ0=sQuery(id+"F0.wireOp",EDGE,"E1");var subQ1=sQuery(id+"F19.wireOp",EDGE,"E133");var subQ2=sQuery(id+"F19.wireOp",EDGE,"E132");var subQ3=sQuery(id+"F19.wireOp",EDGE,"E131");var subQ4=sQuery(id+"F19.wireOp",EDGE,"E130");var subQ5=sQuery(id+"F0.wireOp",EDGE,"E67");Q8=makeQuery(id+"F21.boolean.opBoolean","SPLIT",EDGE,{"disambiguationData":[TD([makeQuery(id+"F21.opPattern","COPY",FACE,{"derivedFrom":makeQuery(id+"F20.opExtrude","CAP_FACE",FACE,{"disambiguationData":[OSD([subQ4,subQ3,subQ2,subQ1])],"isStart":true}),"instanceName":"2"})])],"derivedFrom":makeQuery(id+"F1.opRevolve","SWEPT_EDGE",EDGE,{"disambiguationData":[OSD([subQ0,subQ5])]})});}
            var Q9;
            {var subQ0=sQuery(id+"F0.wireOp",EDGE,"E1");var subQ1=sQuery(id+"F19.wireOp",EDGE,"E133");var subQ2=sQuery(id+"F19.wireOp",EDGE,"E132");var subQ3=sQuery(id+"F19.wireOp",EDGE,"E131");var subQ4=sQuery(id+"F19.wireOp",EDGE,"E130");var subQ5=sQuery(id+"F0.wireOp",EDGE,"E67");Q9=makeQuery(id+"F21.boolean.opBoolean","SPLIT",EDGE,{"disambiguationData":[TD([makeQuery(id+"F21.opPattern","COPY",FACE,{"derivedFrom":makeQuery(id+"F20.opExtrude","CAP_FACE",FACE,{"disambiguationData":[OSD([subQ4,subQ3,subQ2,subQ1])],"isStart":true}),"instanceName":"1"})])],"derivedFrom":makeQuery(id+"F1.opRevolve","SWEPT_EDGE",EDGE,{"disambiguationData":[OSD([subQ0,subQ5])]})});}
            var Q10;
            {var subQ0=sQuery(id+"F0.wireOp",EDGE,"E1");var subQ1=sQuery(id+"F19.wireOp",EDGE,"E133");var subQ2=sQuery(id+"F19.wireOp",EDGE,"E132");var subQ3=sQuery(id+"F19.wireOp",EDGE,"E131");var subQ4=sQuery(id+"F19.wireOp",EDGE,"E130");var subQ5=sQuery(id+"F0.wireOp",EDGE,"E67");Q10=makeQuery(id+"F21.boolean.opBoolean","SPLIT",EDGE,{"disambiguationData":[TD([makeQuery(id+"F20.opExtrude","CAP_FACE",FACE,{"disambiguationData":[OSD([subQ4,subQ3,subQ2,subQ1])],"isStart":true})])],"derivedFrom":makeQuery(id+"F1.opRevolve","SWEPT_EDGE",EDGE,{"disambiguationData":[OSD([subQ0,subQ5])]})});}
            var Q11;
            {var subQ0=sQuery(id+"F0.wireOp",EDGE,"E1");var subQ1=sQuery(id+"F19.wireOp",EDGE,"E133");var subQ2=sQuery(id+"F19.wireOp",EDGE,"E132");var subQ3=sQuery(id+"F19.wireOp",EDGE,"E131");var subQ4=sQuery(id+"F19.wireOp",EDGE,"E130");var subQ5=sQuery(id+"F0.wireOp",EDGE,"E67");Q11=makeQuery(id+"F21.boolean.opBoolean","SPLIT",EDGE,{"disambiguationData":[TD([makeQuery(id+"F20.opExtrude","CAP_FACE",FACE,{"disambiguationData":[OSD([subQ4,subQ3,subQ2,subQ1])],"isStart":false})])],"derivedFrom":makeQuery(id+"F1.opRevolve","SWEPT_EDGE",EDGE,{"disambiguationData":[OSD([subQ0,subQ5])]})});}
            fillet(context, id + "F40", {"entities" : qUnion([Q0, Q1, Q2, Q3, Q4, Q5, Q6, Q7, Q8, Q9, Q10, Q11]), "radius" : 1.27 * mm, "tangentPropagation" : true, "allowEdgeOverflow" : false});
        }
        {
            var Q0;
            Q0=qCreatedBy(makeId("Top.planeOp"),FACE);
            var sketch = newSketch(context, id + "F41", { "sketchPlane" : qUnion([Q0])});
            skLineSegment(sketch, "E207.bottom", {"start": v(-6.35, 186.06) * mm, "end": v(6.35, 186.06) * mm});
            skLineSegment(sketch, "E207.top", {"start": v(-6.35, 154.69) * mm, "end": v(6.35, 154.69) * mm});
            skLineSegment(sketch, "E207.left", {"start": v(-6.35, 186.06) * mm, "end": v(-6.35, 154.69) * mm});
            skLineSegment(sketch, "E207.right", {"start": v(6.35, 186.06) * mm, "end": v(6.35, 154.69) * mm});
            skSolve(sketch);
        }
        {
            var Q0;
            Q0=qSketchRegion(id+"F41",true);
            extrude(context, id + "F42", {"entities" : qUnion([Q0]), "operationType" : NewBodyOperationType.ADD, "depth" : 27.94 * mm});
        }
        {
            var Q0;
            Q0=makeQuery(id+"F42.opExtrude","CAP_FACE",FACE,{"disambiguationData":[OSD([sQuery(id+"F41.wireOp",EDGE,"E207.bottom"),sQuery(id+"F41.wireOp",EDGE,"E207.top"),sQuery(id+"F41.wireOp",EDGE,"E207.left"),sQuery(id+"F41.wireOp",EDGE,"E207.right")])],"isStart":false});
            var sketch = newSketch(context, id + "F43", { "sketchPlane" : qUnion([Q0])});
            skLineSegment(sketch, "E208.bottom", {"start": v(-5.08, 184.78) * mm, "end": v(5.08, 184.78) * mm});
            skLineSegment(sketch, "E208.top", {"start": v(-5.08, 155.96) * mm, "end": v(5.08, 155.96) * mm});
            skLineSegment(sketch, "E208.left", {"start": v(-5.08, 184.78) * mm, "end": v(-5.08, 155.96) * mm});
            skLineSegment(sketch, "E208.right", {"start": v(5.08, 184.78) * mm, "end": v(5.08, 155.96) * mm});
            skLineSegment(sketch, "E209.bottom", {"start": v(-4.45, 184.15) * mm, "end": v(4.44, 184.15) * mm});
            skLineSegment(sketch, "E209.top", {"start": v(-4.45, 156.6) * mm, "end": v(4.44, 156.6) * mm});
            skLineSegment(sketch, "E209.left", {"start": v(-4.45, 184.15) * mm, "end": v(-4.45, 156.6) * mm});
            skLineSegment(sketch, "E209.right", {"start": v(4.44, 184.15) * mm, "end": v(4.44, 156.6) * mm});
            skSolve(sketch);
        }
        {
            var Q0;
            Q0=qSketchRegion(id+"F43",true);
            extrude(context, id + "F44", {"entities" : qUnion([Q0]), "operationType" : NewBodyOperationType.REMOVE, "oppositeDirection" : true, "depth" : 2.54 * mm});
        }
        {
            var Q0;
            Q0=makeQuery(id+"F44.boolean.opBoolean","SPLIT",FACE,{"disambiguationData":[TD([makeQuery(id+"F44.opExtrude","SWEPT_FACE",FACE,{"disambiguationData":[OSD([sQuery(id+"F43.wireOp",EDGE,"E209.bottom")])]})])],"derivedFrom":makeQuery(id+"F42.opExtrude","CAP_FACE",FACE,{"disambiguationData":[OSD([sQuery(id+"F41.wireOp",EDGE,"E207.bottom"),sQuery(id+"F41.wireOp",EDGE,"E207.top"),sQuery(id+"F41.wireOp",EDGE,"E207.left"),sQuery(id+"F41.wireOp",EDGE,"E207.right")])],"isStart":false})});
            var sketch = newSketch(context, id + "F45", { "sketchPlane" : qUnion([Q0])});
            skLineSegment(sketch, "E210", {"start": v(0, 184.15) * mm, "end": v(0, 156.6) * mm, "construction": true});
            skLineSegment(sketch, "E211", {"start": v(-4.45, 179.7) * mm, "end": v(4.44, 179.7) * mm, "construction": true});
            skLineSegment(sketch, "E212", {"start": v(-4.45, 161.04) * mm, "end": v(4.44, 161.04) * mm, "construction": true});
            skLineSegment(sketch, "E213.rect.bottom", {"start": v(1.61, 179.45) * mm, "end": v(-1.61, 179.45) * mm});
            skLineSegment(sketch, "E213.rect.top", {"start": v(1.61, 179.7) * mm, "end": v(-1.61, 179.7) * mm});
            skPoint(sketch, "E213.rect.middle", {"position": v(0, 179.58) * mm});
            skLineSegment(sketch, "E214.1.0.0", {"start": v(1.9, 178.82) * mm, "end": v(-1.9, 178.82) * mm});
            skLineSegment(sketch, "E214.1.0.1", {"start": v(-1.9, 178.82) * mm, "end": v(-1.9, 179.07) * mm});
            skLineSegment(sketch, "E214.1.0.2", {"start": v(1.9, 178.82) * mm, "end": v(1.9, 179.07) * mm});
            skLineSegment(sketch, "E214.1.0.3", {"start": v(1.9, 179.07) * mm, "end": v(-1.9, 179.07) * mm});
            skLineSegment(sketch, "E214.2.0.0", {"start": v(1.9, 178.18) * mm, "end": v(-1.9, 178.18) * mm});
            skLineSegment(sketch, "E214.2.0.1", {"start": v(-1.9, 178.18) * mm, "end": v(-1.9, 178.44) * mm});
            skLineSegment(sketch, "E214.2.0.2", {"start": v(1.9, 178.18) * mm, "end": v(1.9, 178.44) * mm});
            skLineSegment(sketch, "E214.2.0.3", {"start": v(1.9, 178.44) * mm, "end": v(-1.9, 178.44) * mm});
            skLineSegment(sketch, "E214.3.0.0", {"start": v(1.9, 177.55) * mm, "end": v(-1.9, 177.55) * mm});
            skLineSegment(sketch, "E214.3.0.1", {"start": v(-1.9, 177.55) * mm, "end": v(-1.9, 177.8) * mm});
            skLineSegment(sketch, "E214.3.0.2", {"start": v(1.9, 177.55) * mm, "end": v(1.9, 177.8) * mm});
            skLineSegment(sketch, "E214.3.0.3", {"start": v(1.9, 177.8) * mm, "end": v(-1.9, 177.8) * mm});
            skLineSegment(sketch, "E214.4.0.0", {"start": v(1.9, 176.91) * mm, "end": v(-1.9, 176.91) * mm});
            skLineSegment(sketch, "E214.4.0.1", {"start": v(-1.9, 176.91) * mm, "end": v(-1.9, 177.17) * mm});
            skLineSegment(sketch, "E214.4.0.2", {"start": v(1.9, 176.91) * mm, "end": v(1.9, 177.17) * mm});
            skLineSegment(sketch, "E214.4.0.3", {"start": v(1.9, 177.17) * mm, "end": v(-1.9, 177.17) * mm});
            skLineSegment(sketch, "E214.5.0.0", {"start": v(1.9, 176.28) * mm, "end": v(-1.9, 176.28) * mm});
            skLineSegment(sketch, "E214.5.0.1", {"start": v(-1.9, 176.28) * mm, "end": v(-1.9, 176.53) * mm});
            skLineSegment(sketch, "E214.5.0.2", {"start": v(1.9, 176.28) * mm, "end": v(1.9, 176.53) * mm});
            skLineSegment(sketch, "E214.5.0.3", {"start": v(1.9, 176.53) * mm, "end": v(-1.9, 176.53) * mm});
            skLineSegment(sketch, "E214.6.0.0", {"start": v(1.9, 175.64) * mm, "end": v(-1.9, 175.64) * mm});
            skLineSegment(sketch, "E214.6.0.1", {"start": v(-1.9, 175.64) * mm, "end": v(-1.9, 175.9) * mm});
            skLineSegment(sketch, "E214.6.0.2", {"start": v(1.9, 175.64) * mm, "end": v(1.9, 175.9) * mm});
            skLineSegment(sketch, "E214.6.0.3", {"start": v(1.9, 175.9) * mm, "end": v(-1.9, 175.9) * mm});
            skLineSegment(sketch, "E214.7.0.0", {"start": v(1.9, 175) * mm, "end": v(-1.9, 175) * mm});
            skLineSegment(sketch, "E214.7.0.1", {"start": v(-1.9, 175) * mm, "end": v(-1.9, 175.26) * mm});
            skLineSegment(sketch, "E214.7.0.2", {"start": v(1.9, 175) * mm, "end": v(1.9, 175.26) * mm});
            skLineSegment(sketch, "E214.7.0.3", {"start": v(1.9, 175.26) * mm, "end": v(-1.9, 175.26) * mm});
            skLineSegment(sketch, "E214.8.0.0", {"start": v(1.9, 174.37) * mm, "end": v(-1.91, 174.37) * mm});
            skLineSegment(sketch, "E214.8.0.1", {"start": v(-1.91, 174.37) * mm, "end": v(-1.91, 174.63) * mm});
            skLineSegment(sketch, "E214.8.0.2", {"start": v(1.9, 174.37) * mm, "end": v(1.9, 174.63) * mm});
            skLineSegment(sketch, "E214.8.0.3", {"start": v(1.9, 174.63) * mm, "end": v(-1.91, 174.63) * mm});
            skLineSegment(sketch, "E214.9.0.0", {"start": v(1.9, 173.74) * mm, "end": v(-1.91, 173.74) * mm});
            skLineSegment(sketch, "E214.9.0.1", {"start": v(-1.91, 173.74) * mm, "end": v(-1.91, 174) * mm});
            skLineSegment(sketch, "E214.9.0.2", {"start": v(1.9, 173.74) * mm, "end": v(1.9, 174) * mm});
            skLineSegment(sketch, "E214.9.0.3", {"start": v(1.9, 174) * mm, "end": v(-1.91, 174) * mm});
            skLineSegment(sketch, "E214.10.0.0", {"start": v(1.9, 173.1) * mm, "end": v(-1.91, 173.1) * mm});
            skLineSegment(sketch, "E214.10.0.1", {"start": v(-1.91, 173.1) * mm, "end": v(-1.91, 173.36) * mm});
            skLineSegment(sketch, "E214.10.0.2", {"start": v(1.9, 173.1) * mm, "end": v(1.9, 173.36) * mm});
            skLineSegment(sketch, "E214.10.0.3", {"start": v(1.9, 173.36) * mm, "end": v(-1.91, 173.36) * mm});
            skLineSegment(sketch, "E214.11.0.0", {"start": v(1.9, 172.47) * mm, "end": v(-1.91, 172.47) * mm});
            skLineSegment(sketch, "E214.11.0.1", {"start": v(-1.91, 172.47) * mm, "end": v(-1.91, 172.72) * mm});
            skLineSegment(sketch, "E214.11.0.2", {"start": v(1.9, 172.47) * mm, "end": v(1.9, 172.72) * mm});
            skLineSegment(sketch, "E214.11.0.3", {"start": v(1.9, 172.72) * mm, "end": v(-1.91, 172.72) * mm});
            skLineSegment(sketch, "E214.12.0.0", {"start": v(1.9, 171.83) * mm, "end": v(-1.91, 171.83) * mm});
            skLineSegment(sketch, "E214.12.0.1", {"start": v(-1.91, 171.83) * mm, "end": v(-1.91, 172.09) * mm});
            skLineSegment(sketch, "E214.12.0.2", {"start": v(1.9, 171.83) * mm, "end": v(1.9, 172.09) * mm});
            skLineSegment(sketch, "E214.12.0.3", {"start": v(1.9, 172.09) * mm, "end": v(-1.91, 172.09) * mm});
            skLineSegment(sketch, "E214.13.0.0", {"start": v(1.9, 171.2) * mm, "end": v(-1.91, 171.2) * mm});
            skLineSegment(sketch, "E214.13.0.1", {"start": v(-1.91, 171.2) * mm, "end": v(-1.91, 171.45) * mm});
            skLineSegment(sketch, "E214.13.0.2", {"start": v(1.9, 171.2) * mm, "end": v(1.9, 171.45) * mm});
            skLineSegment(sketch, "E214.13.0.3", {"start": v(1.9, 171.45) * mm, "end": v(-1.91, 171.45) * mm});
            skLineSegment(sketch, "E214.14.0.0", {"start": v(1.9, 170.56) * mm, "end": v(-1.91, 170.56) * mm});
            skLineSegment(sketch, "E214.14.0.1", {"start": v(-1.91, 170.56) * mm, "end": v(-1.91, 170.82) * mm});
            skLineSegment(sketch, "E214.14.0.2", {"start": v(1.9, 170.56) * mm, "end": v(1.9, 170.82) * mm});
            skLineSegment(sketch, "E214.14.0.3", {"start": v(1.9, 170.82) * mm, "end": v(-1.91, 170.82) * mm});
            skLineSegment(sketch, "E214.15.0.0", {"start": v(1.9, 169.93) * mm, "end": v(-1.91, 169.93) * mm});
            skLineSegment(sketch, "E214.15.0.1", {"start": v(-1.91, 169.93) * mm, "end": v(-1.91, 170.18) * mm});
            skLineSegment(sketch, "E214.15.0.2", {"start": v(1.9, 169.93) * mm, "end": v(1.9, 170.18) * mm});
            skLineSegment(sketch, "E214.15.0.3", {"start": v(1.9, 170.18) * mm, "end": v(-1.91, 170.18) * mm});
            skLineSegment(sketch, "E214.16.0.0", {"start": v(1.9, 169.3) * mm, "end": v(-1.92, 169.3) * mm});
            skLineSegment(sketch, "E214.16.0.1", {"start": v(-1.92, 169.3) * mm, "end": v(-1.92, 169.55) * mm});
            skLineSegment(sketch, "E214.16.0.2", {"start": v(1.9, 169.3) * mm, "end": v(1.9, 169.55) * mm});
            skLineSegment(sketch, "E214.16.0.3", {"start": v(1.9, 169.55) * mm, "end": v(-1.92, 169.55) * mm});
            skLineSegment(sketch, "E214.17.0.0", {"start": v(1.9, 168.66) * mm, "end": v(-1.92, 168.66) * mm});
            skLineSegment(sketch, "E214.17.0.1", {"start": v(-1.92, 168.66) * mm, "end": v(-1.92, 168.91) * mm});
            skLineSegment(sketch, "E214.17.0.2", {"start": v(1.9, 168.66) * mm, "end": v(1.9, 168.91) * mm});
            skLineSegment(sketch, "E214.17.0.3", {"start": v(1.9, 168.91) * mm, "end": v(-1.92, 168.91) * mm});
            skLineSegment(sketch, "E214.18.0.0", {"start": v(1.9, 168.02) * mm, "end": v(-1.92, 168.02) * mm});
            skLineSegment(sketch, "E214.18.0.1", {"start": v(-1.92, 168.02) * mm, "end": v(-1.92, 168.28) * mm});
            skLineSegment(sketch, "E214.18.0.2", {"start": v(1.9, 168.02) * mm, "end": v(1.9, 168.28) * mm});
            skLineSegment(sketch, "E214.18.0.3", {"start": v(1.9, 168.28) * mm, "end": v(-1.92, 168.28) * mm});
            skLineSegment(sketch, "E214.19.0.0", {"start": v(1.9, 167.39) * mm, "end": v(-1.92, 167.39) * mm});
            skLineSegment(sketch, "E214.19.0.1", {"start": v(-1.92, 167.39) * mm, "end": v(-1.92, 167.64) * mm});
            skLineSegment(sketch, "E214.19.0.2", {"start": v(1.9, 167.39) * mm, "end": v(1.9, 167.64) * mm});
            skLineSegment(sketch, "E214.19.0.3", {"start": v(1.9, 167.64) * mm, "end": v(-1.92, 167.64) * mm});
            skLineSegment(sketch, "E214.20.0.0", {"start": v(1.9, 166.75) * mm, "end": v(-1.92, 166.75) * mm});
            skLineSegment(sketch, "E214.20.0.1", {"start": v(-1.92, 166.75) * mm, "end": v(-1.92, 167) * mm});
            skLineSegment(sketch, "E214.20.0.2", {"start": v(1.9, 166.75) * mm, "end": v(1.9, 167) * mm});
            skLineSegment(sketch, "E214.20.0.3", {"start": v(1.9, 167) * mm, "end": v(-1.92, 167) * mm});
            skLineSegment(sketch, "E214.21.0.0", {"start": v(1.9, 166.12) * mm, "end": v(-1.92, 166.12) * mm});
            skLineSegment(sketch, "E214.21.0.1", {"start": v(-1.92, 166.12) * mm, "end": v(-1.92, 166.37) * mm});
            skLineSegment(sketch, "E214.21.0.2", {"start": v(1.9, 166.12) * mm, "end": v(1.9, 166.37) * mm});
            skLineSegment(sketch, "E214.21.0.3", {"start": v(1.9, 166.37) * mm, "end": v(-1.92, 166.37) * mm});
            skLineSegment(sketch, "E214.22.0.0", {"start": v(1.9, 165.48) * mm, "end": v(-1.92, 165.48) * mm});
            skLineSegment(sketch, "E214.22.0.1", {"start": v(-1.92, 165.48) * mm, "end": v(-1.92, 165.74) * mm});
            skLineSegment(sketch, "E214.22.0.2", {"start": v(1.9, 165.48) * mm, "end": v(1.9, 165.74) * mm});
            skLineSegment(sketch, "E214.22.0.3", {"start": v(1.9, 165.74) * mm, "end": v(-1.92, 165.74) * mm});
            skLineSegment(sketch, "E214.23.0.0", {"start": v(1.89, 164.85) * mm, "end": v(-1.92, 164.85) * mm});
            skLineSegment(sketch, "E214.23.0.1", {"start": v(-1.92, 164.85) * mm, "end": v(-1.92, 165.1) * mm});
            skLineSegment(sketch, "E214.23.0.2", {"start": v(1.89, 164.85) * mm, "end": v(1.89, 165.1) * mm});
            skLineSegment(sketch, "E214.23.0.3", {"start": v(1.89, 165.1) * mm, "end": v(-1.92, 165.1) * mm});
            skLineSegment(sketch, "E214.24.0.0", {"start": v(1.89, 164.21) * mm, "end": v(-1.92, 164.21) * mm});
            skLineSegment(sketch, "E214.24.0.1", {"start": v(-1.92, 164.21) * mm, "end": v(-1.92, 164.47) * mm});
            skLineSegment(sketch, "E214.24.0.2", {"start": v(1.89, 164.21) * mm, "end": v(1.89, 164.47) * mm});
            skLineSegment(sketch, "E214.24.0.3", {"start": v(1.89, 164.47) * mm, "end": v(-1.92, 164.47) * mm});
            skLineSegment(sketch, "E214.25.0.0", {"start": v(1.89, 163.58) * mm, "end": v(-1.92, 163.58) * mm});
            skLineSegment(sketch, "E214.25.0.1", {"start": v(-1.92, 163.58) * mm, "end": v(-1.92, 163.83) * mm});
            skLineSegment(sketch, "E214.25.0.2", {"start": v(1.89, 163.58) * mm, "end": v(1.89, 163.83) * mm});
            skLineSegment(sketch, "E214.25.0.3", {"start": v(1.89, 163.83) * mm, "end": v(-1.92, 163.83) * mm});
            skLineSegment(sketch, "E214.26.0.0", {"start": v(1.89, 162.94) * mm, "end": v(-1.92, 162.94) * mm});
            skLineSegment(sketch, "E214.26.0.1", {"start": v(-1.92, 162.94) * mm, "end": v(-1.92, 163.2) * mm});
            skLineSegment(sketch, "E214.26.0.2", {"start": v(1.89, 162.94) * mm, "end": v(1.89, 163.2) * mm});
            skLineSegment(sketch, "E214.26.0.3", {"start": v(1.89, 163.2) * mm, "end": v(-1.92, 163.2) * mm});
            skLineSegment(sketch, "E214.27.0.0", {"start": v(1.89, 162.3) * mm, "end": v(-1.92, 162.3) * mm});
            skLineSegment(sketch, "E214.27.0.1", {"start": v(-1.92, 162.3) * mm, "end": v(-1.92, 162.56) * mm});
            skLineSegment(sketch, "E214.27.0.2", {"start": v(1.89, 162.3) * mm, "end": v(1.89, 162.56) * mm});
            skLineSegment(sketch, "E214.27.0.3", {"start": v(1.89, 162.56) * mm, "end": v(-1.92, 162.56) * mm});
            skLineSegment(sketch, "E214.28.0.0", {"start": v(1.89, 161.67) * mm, "end": v(-1.92, 161.67) * mm});
            skLineSegment(sketch, "E214.28.0.1", {"start": v(-1.92, 161.67) * mm, "end": v(-1.92, 161.93) * mm});
            skLineSegment(sketch, "E214.28.0.2", {"start": v(1.89, 161.67) * mm, "end": v(1.89, 161.93) * mm});
            skLineSegment(sketch, "E214.28.0.3", {"start": v(1.89, 161.93) * mm, "end": v(-1.92, 161.93) * mm});
            skLineSegment(sketch, "E214.29.0.0", {"start": v(1.6, 161.04) * mm, "end": v(-1.63, 161.04) * mm});
            skLineSegment(sketch, "E214.29.0.3", {"start": v(1.6, 161.3) * mm, "end": v(-1.63, 161.3) * mm});
            skLineSegment(sketch, "E214.direction1", {"start": v(-1.9, 179.45) * mm, "end": v(-1.9, 178.82) * mm, "construction": true});
            skArc(sketch, "E215", {"start": v(-1.61, 179.7) * mm, "mid": v(-2.22, 179.58) * mm, "end": v(-1.61, 179.45) * mm});
            skArc(sketch, "E216", {"start": v(1.61, 179.45) * mm, "mid": v(2.22, 179.58) * mm, "end": v(1.61, 179.7) * mm});
            skArc(sketch, "E217", {"start": v(-1.63, 161.3) * mm, "mid": v(-2.24, 161.16) * mm, "end": v(-1.63, 161.04) * mm});
            skArc(sketch, "E218", {"start": v(1.6, 161.04) * mm, "mid": v(2.2, 161.16) * mm, "end": v(1.6, 161.3) * mm});
            skPoint(sketch, "E213.rect.right.end.orphan", {"position": v(-1.9, 179.7) * mm});
            skPoint(sketch, "E219.orphan", {"position": v(1.9, 179.7) * mm});
            skPoint(sketch, "E213.rect.left.start.orphan", {"position": v(1.9, 179.45) * mm});
            skPoint(sketch, "E220.orphan", {"position": v(-1.92, 161.04) * mm});
            skPoint(sketch, "E214.29.0.1.end.orphan", {"position": v(-1.92, 161.3) * mm});
            skPoint(sketch, "E221.orphan", {"position": v(1.89, 161.3) * mm});
            skPoint(sketch, "E214.29.0.2.start.orphan", {"position": v(1.89, 161.04) * mm});
            skLineSegment(sketch, "E222.rect.bottom", {"start": v(3.5, 180.6) * mm, "end": v(-3.5, 180.6) * mm});
            skLineSegment(sketch, "E222.rect.top", {"start": v(3.5, 183.26) * mm, "end": v(-3.5, 183.26) * mm});
            skLineSegment(sketch, "E222.rect.left", {"start": v(3.5, 180.6) * mm, "end": v(3.5, 183.26) * mm});
            skLineSegment(sketch, "E222.rect.right", {"start": v(-3.5, 180.6) * mm, "end": v(-3.5, 183.26) * mm});
            skPoint(sketch, "E222.rect.middle", {"position": v(0, 181.93) * mm});
            skLineSegment(sketch, "E223.rect.bottom", {"start": v(3.24, 180.85) * mm, "end": v(-3.24, 180.85) * mm});
            skLineSegment(sketch, "E223.rect.top", {"start": v(3.24, 183) * mm, "end": v(-3.24, 183) * mm});
            skLineSegment(sketch, "E223.rect.left", {"start": v(3.24, 180.85) * mm, "end": v(3.24, 183) * mm});
            skLineSegment(sketch, "E223.rect.right", {"start": v(-3.24, 180.85) * mm, "end": v(-3.24, 183) * mm});
            skLineSegment(sketch, "E224.rect.bottom", {"start": v(3.5, 157.48) * mm, "end": v(-3.5, 157.48) * mm});
            skLineSegment(sketch, "E224.rect.top", {"start": v(3.5, 160.15) * mm, "end": v(-3.5, 160.15) * mm});
            skLineSegment(sketch, "E224.rect.left", {"start": v(3.5, 157.48) * mm, "end": v(3.5, 160.15) * mm});
            skLineSegment(sketch, "E224.rect.right", {"start": v(-3.5, 157.48) * mm, "end": v(-3.5, 160.15) * mm});
            skPoint(sketch, "E224.rect.middle", {"position": v(0, 158.81) * mm});
            skLineSegment(sketch, "E225.rect.bottom", {"start": v(3.24, 157.73) * mm, "end": v(-3.24, 157.73) * mm});
            skLineSegment(sketch, "E225.rect.top", {"start": v(3.24, 159.9) * mm, "end": v(-3.24, 159.9) * mm});
            skLineSegment(sketch, "E225.rect.left", {"start": v(3.24, 157.73) * mm, "end": v(3.24, 159.9) * mm});
            skLineSegment(sketch, "E225.rect.right", {"start": v(-3.24, 157.73) * mm, "end": v(-3.24, 159.9) * mm});
            skSolve(sketch);
        }
        {
            var Q0;
            Q0=qSketchRegion(id+"F45",true);
            extrude(context, id + "F46", {"entities" : qUnion([Q0]), "operationType" : NewBodyOperationType.REMOVE, "oppositeDirection" : true, "depth" : 1.27 * mm});
        }
        {
            var Q0;
            Q0=makeQuery(id+"F42.opExtrude","CAP_EDGE",EDGE,{"disambiguationData":[OSD([sQuery(id+"F41.wireOp",EDGE,"E207.left")])],"isStart":false});
            var Q1;
            Q1=makeQuery(id+"F42.opExtrude","CAP_EDGE",EDGE,{"disambiguationData":[OSD([sQuery(id+"F41.wireOp",EDGE,"E207.top")])],"isStart":false});
            var Q2;
            Q2=makeQuery(id+"F42.opExtrude","CAP_EDGE",EDGE,{"disambiguationData":[OSD([sQuery(id+"F41.wireOp",EDGE,"E207.right")])],"isStart":false});
            var Q3;
            Q3=makeQuery(id+"F42.opExtrude","CAP_EDGE",EDGE,{"disambiguationData":[OSD([sQuery(id+"F41.wireOp",EDGE,"E207.bottom")])],"isStart":false});
            chamfer(context, id + "F47", {"entities" : qUnion([Q0, Q1, Q2, Q3]), "width" : 0.64 * mm, "tangentPropagation" : true});
        }
    });
